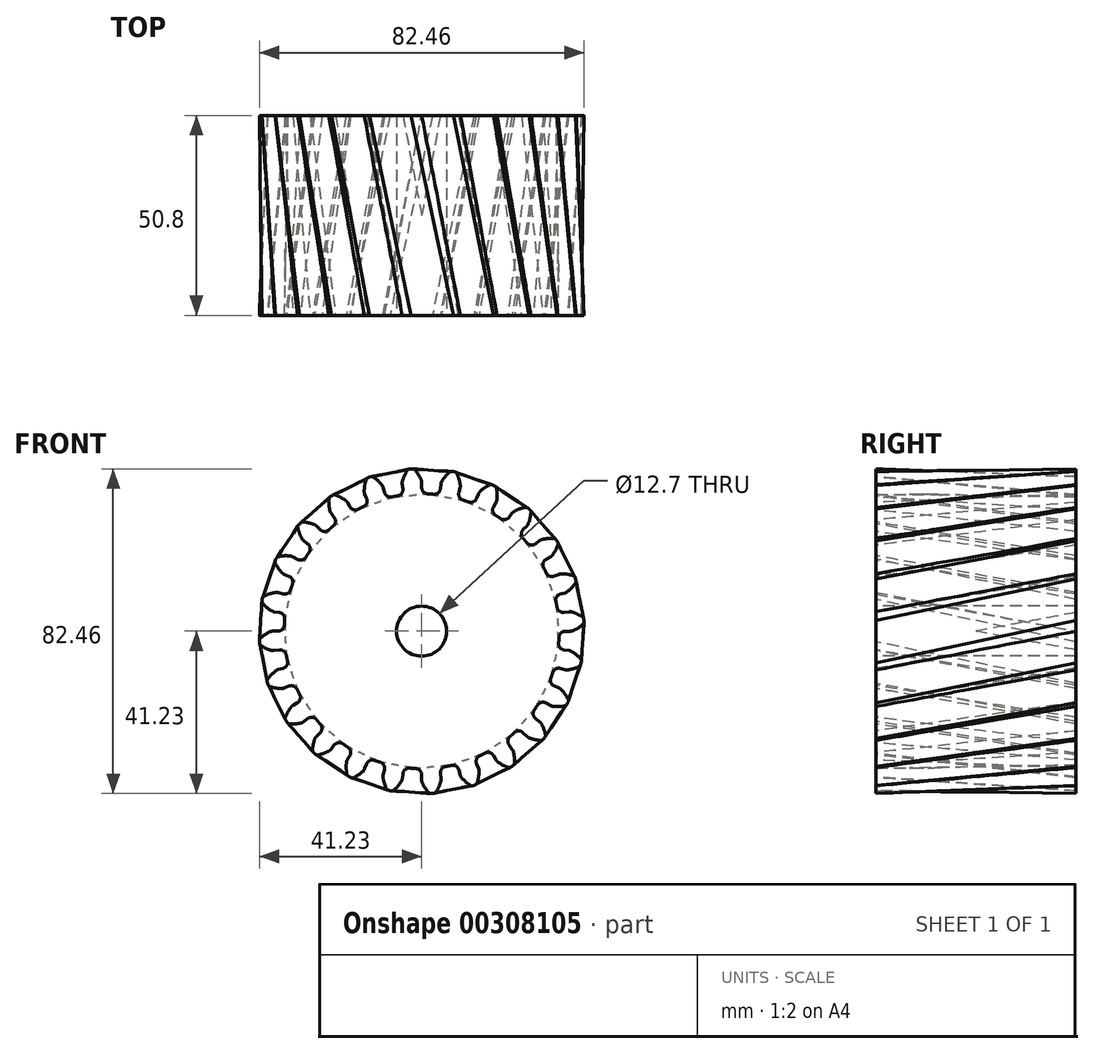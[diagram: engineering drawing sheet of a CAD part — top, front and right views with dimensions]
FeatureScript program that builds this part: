
annotation { "Feature Type Name" : "Feature", "Feature Type Description" : "" }
export const myFeature = defineFeature(function(context is Context, id is Id, definition is map)
    precondition{}
    {
        {
            var Q0;
            Q0=qCreatedBy(makeId("Front.planeOp"),FACE);
            var sketch = newSketch(context, id + "F0", { "sketchPlane" : qUnion([Q0])});
            skArc(sketch, "E0", {"start": v(-6.07, 34.4) * mm, "mid": v(-6.81, 34.25) * mm, "end": v(-7.56, 34.1) * mm});
            skArc(sketch, "E1.trimOffspring", {"start": v(-0.12, 38.41) * mm, "mid": v(-0.85, 39.8) * mm, "end": v(-1.8, 41.06) * mm});
            skLineSegment(sketch, "E2", {"start": v(-2.18, 41.23) * mm, "end": v(-2.7, 41.23) * mm});
            skLineSegment(sketch, "E3", {"start": v(0, 37.8) * mm, "end": v(0, 36.48) * mm});
            skLineSegment(sketch, "E4.MirrorCS", {"start": v(-3.22, 41.16) * mm, "end": v(-2.7, 41.23) * mm});
            skArc(sketch, "E5.MirrorCS", {"start": v(-4.9, 38.1) * mm, "mid": v(-4.35, 39.58) * mm, "end": v(-3.57, 40.95) * mm});
            skLineSegment(sketch, "E6.MirrorCS", {"start": v(-4.94, 37.47) * mm, "end": v(-4.77, 36.16) * mm});
            skPoint(sketch, "E7.visualSharp", {"position": v(-3.44, 41.13) * mm});
            skArc(sketch, "E7.filletArc", {"start": v(-3.22, 41.16) * mm, "mid": v(-3.41, 41.1) * mm, "end": v(-3.57, 40.95) * mm});
            skPoint(sketch, "E8.visualSharp", {"position": v(-1.96, 41.23) * mm});
            skArc(sketch, "E8.filletArc", {"start": v(-1.8, 41.06) * mm, "mid": v(-1.98, 41.18) * mm, "end": v(-2.18, 41.23) * mm});
            skPoint(sketch, "E9.visualSharp", {"position": v(-4.98, 37.77) * mm});
            skArc(sketch, "E9.filletArc", {"start": v(-4.9, 38.1) * mm, "mid": v(-4.95, 37.79) * mm, "end": v(-4.94, 37.47) * mm});
            skPoint(sketch, "E10.visualSharp", {"position": v(0, 38.1) * mm});
            skArc(sketch, "E10.filletArc", {"start": v(0, 37.8) * mm, "mid": v(-0.02, 38.1) * mm, "end": v(-0.12, 38.41) * mm});
            skPoint(sketch, "E11.visualSharp", {"position": v(0, 34.92) * mm});
            skArc(sketch, "E11.filletArc", {"start": v(0, 36.48) * mm, "mid": v(0.45, 35.38) * mm, "end": v(1.53, 34.9) * mm});
            skPoint(sketch, "E12.visualSharp", {"position": v(-4.57, 34.63) * mm});
            skArc(sketch, "E12.filletArc", {"start": v(-6.07, 34.4) * mm, "mid": v(-5.06, 35.02) * mm, "end": v(-4.77, 36.16) * mm});
            skLineSegment(sketch, "E13.1.0", {"start": v(-14.47, 34.91) * mm, "end": v(-13.97, 33.7) * mm});
            skArc(sketch, "E13.1.1", {"start": v(-14.76, 31.65) * mm, "mid": v(-13.95, 32.51) * mm, "end": v(-13.97, 33.7) * mm});
            skLineSegment(sketch, "E13.1.2", {"start": v(-9.77, 36.5) * mm, "end": v(-9.43, 35.24) * mm});
            skArc(sketch, "E13.1.3", {"start": v(-9.43, 35.24) * mm, "mid": v(-8.72, 34.3) * mm, "end": v(-7.56, 34.1) * mm});
            skArc(sketch, "E13.1.4", {"start": v(-14.6, 35.53) * mm, "mid": v(-14.56, 35.22) * mm, "end": v(-14.47, 34.91) * mm});
            skArc(sketch, "E13.1.5", {"start": v(-14.6, 35.53) * mm, "mid": v(-14.45, 37.1) * mm, "end": v(-14.04, 38.63) * mm});
            skArc(sketch, "E13.1.6", {"start": v(-13.76, 38.93) * mm, "mid": v(-13.93, 38.8) * mm, "end": v(-14.04, 38.63) * mm});
            skLineSegment(sketch, "E13.1.7", {"start": v(-13.76, 38.93) * mm, "end": v(-13.28, 39.12) * mm});
            skLineSegment(sketch, "E13.1.8", {"start": v(-12.78, 39.26) * mm, "end": v(-13.28, 39.12) * mm});
            skArc(sketch, "E13.1.9", {"start": v(-12.37, 39.2) * mm, "mid": v(-12.57, 39.27) * mm, "end": v(-12.78, 39.26) * mm});
            skArc(sketch, "E13.1.10", {"start": v(-10.06, 37.07) * mm, "mid": v(-11.13, 38.23) * mm, "end": v(-12.37, 39.2) * mm});
            skArc(sketch, "E13.1.11", {"start": v(-9.77, 36.5) * mm, "mid": v(-9.89, 36.8) * mm, "end": v(-10.06, 37.07) * mm});
            skLineSegment(sketch, "E13.2.0", {"start": v(-23.01, 29.98) * mm, "end": v(-22.21, 28.93) * mm});
            skArc(sketch, "E13.2.1", {"start": v(-22.45, 26.75) * mm, "mid": v(-21.9, 27.8) * mm, "end": v(-22.21, 28.93) * mm});
            skLineSegment(sketch, "E13.2.2", {"start": v(-18.89, 32.73) * mm, "end": v(-18.23, 31.6) * mm});
            skArc(sketch, "E13.2.3", {"start": v(-18.23, 31.6) * mm, "mid": v(-17.3, 30.86) * mm, "end": v(-16.12, 30.98) * mm});
            skArc(sketch, "E13.2.4", {"start": v(-23.3, 30.55) * mm, "mid": v(-23.18, 30.25) * mm, "end": v(-23.01, 29.98) * mm});
            skArc(sketch, "E13.2.5", {"start": v(-23.3, 30.55) * mm, "mid": v(-23.56, 32.1) * mm, "end": v(-23.56, 33.68) * mm});
            skArc(sketch, "E13.2.6", {"start": v(-23.36, 34.04) * mm, "mid": v(-23.5, 33.88) * mm, "end": v(-23.56, 33.68) * mm});
            skLineSegment(sketch, "E13.2.7", {"start": v(-23.36, 34.04) * mm, "end": v(-22.95, 34.35) * mm});
            skLineSegment(sketch, "E13.2.8", {"start": v(-22.5, 34.61) * mm, "end": v(-22.95, 34.35) * mm});
            skArc(sketch, "E13.2.9", {"start": v(-22.1, 34.66) * mm, "mid": v(-22.3, 34.68) * mm, "end": v(-22.5, 34.61) * mm});
            skArc(sketch, "E13.2.10", {"start": v(-19.3, 33.2) * mm, "mid": v(-20.64, 34.05) * mm, "end": v(-22.1, 34.66) * mm});
            skArc(sketch, "E13.2.11", {"start": v(-18.89, 32.73) * mm, "mid": v(-19.07, 33) * mm, "end": v(-19.3, 33.2) * mm});
            skLineSegment(sketch, "E14.2.3.0", {"start": v(-29.99, 23) * mm, "end": v(-28.94, 22.2) * mm});
            skArc(sketch, "E14.3.3.0", {"start": v(-28.61, 20.03) * mm, "mid": v(-28.34, 21.18) * mm, "end": v(-28.94, 22.2) * mm});
            skLineSegment(sketch, "E14.7.3.0", {"start": v(-26.72, 26.73) * mm, "end": v(-25.79, 25.8) * mm});
            skArc(sketch, "E14.10.3.0", {"start": v(-25.79, 25.8) * mm, "mid": v(-24.7, 25.34) * mm, "end": v(-23.6, 25.75) * mm});
            skArc(sketch, "E14.14.3.0", {"start": v(-30.4, 23.48) * mm, "mid": v(-30.22, 23.22) * mm, "end": v(-29.99, 23) * mm});
            skArc(sketch, "E14.18.3.0", {"start": v(-30.4, 23.48) * mm, "mid": v(-31.06, 24.9) * mm, "end": v(-31.48, 26.43) * mm});
            skArc(sketch, "E14.22.3.0", {"start": v(-31.38, 26.83) * mm, "mid": v(-31.47, 26.64) * mm, "end": v(-31.48, 26.43) * mm});
            skLineSegment(sketch, "E14.26.3.0", {"start": v(-31.38, 26.83) * mm, "end": v(-31.06, 27.24) * mm});
            skLineSegment(sketch, "E14.29.3.0", {"start": v(-30.7, 27.6) * mm, "end": v(-31.06, 27.24) * mm});
            skArc(sketch, "E14.32.3.0", {"start": v(-30.31, 27.76) * mm, "mid": v(-30.52, 27.72) * mm, "end": v(-30.7, 27.6) * mm});
            skArc(sketch, "E14.36.3.0", {"start": v(-27.25, 27.08) * mm, "mid": v(-28.75, 27.54) * mm, "end": v(-30.31, 27.76) * mm});
            skArc(sketch, "E14.40.3.0", {"start": v(-26.72, 26.73) * mm, "mid": v(-26.96, 26.93) * mm, "end": v(-27.25, 27.08) * mm});
            skLineSegment(sketch, "E14.2.4.0", {"start": v(-34.92, 14.45) * mm, "end": v(-33.7, 13.95) * mm});
            skArc(sketch, "E14.3.4.0", {"start": v(-32.82, 11.94) * mm, "mid": v(-32.86, 13.12) * mm, "end": v(-33.7, 13.95) * mm});
            skLineSegment(sketch, "E14.7.4.0", {"start": v(-32.72, 18.9) * mm, "end": v(-31.59, 18.25) * mm});
            skArc(sketch, "E14.10.4.0", {"start": v(-31.59, 18.25) * mm, "mid": v(-30.42, 18.08) * mm, "end": v(-29.45, 18.77) * mm});
            skArc(sketch, "E14.14.4.0", {"start": v(-35.44, 14.8) * mm, "mid": v(-35.2, 14.6) * mm, "end": v(-34.92, 14.45) * mm});
            skArc(sketch, "E14.18.4.0", {"start": v(-35.44, 14.8) * mm, "mid": v(-36.45, 16.02) * mm, "end": v(-37.24, 17.38) * mm});
            skArc(sketch, "E14.22.4.0", {"start": v(-37.25, 17.8) * mm, "mid": v(-37.3, 17.59) * mm, "end": v(-37.24, 17.38) * mm});
            skLineSegment(sketch, "E14.26.4.0", {"start": v(-37.25, 17.8) * mm, "end": v(-37.06, 18.27) * mm});
            skLineSegment(sketch, "E14.29.4.0", {"start": v(-36.8, 18.72) * mm, "end": v(-37.06, 18.27) * mm});
            skArc(sketch, "E14.32.4.0", {"start": v(-36.46, 18.96) * mm, "mid": v(-36.66, 18.88) * mm, "end": v(-36.8, 18.72) * mm});
            skArc(sketch, "E14.36.4.0", {"start": v(-33.33, 19.1) * mm, "mid": v(-34.9, 19.16) * mm, "end": v(-36.46, 18.96) * mm});
            skArc(sketch, "E14.40.4.0", {"start": v(-32.72, 18.9) * mm, "mid": v(-33.01, 19.03) * mm, "end": v(-33.33, 19.1) * mm});
            skLineSegment(sketch, "E14.2.5.0", {"start": v(-37.47, 4.92) * mm, "end": v(-36.17, 4.75) * mm});
            skArc(sketch, "E14.3.5.0", {"start": v(-34.8, 3.04) * mm, "mid": v(-35.14, 4.17) * mm, "end": v(-36.17, 4.75) * mm});
            skLineSegment(sketch, "E14.7.5.0", {"start": v(-36.5, 9.79) * mm, "end": v(-35.23, 9.45) * mm});
            skArc(sketch, "E14.10.5.0", {"start": v(-35.23, 9.45) * mm, "mid": v(-34.06, 9.6) * mm, "end": v(-33.3, 10.5) * mm});
            skArc(sketch, "E14.14.5.0", {"start": v(-38.07, 5.13) * mm, "mid": v(-37.78, 5) * mm, "end": v(-37.47, 4.92) * mm});
            skArc(sketch, "E14.18.5.0", {"start": v(-38.07, 5.13) * mm, "mid": v(-39.36, 6.04) * mm, "end": v(-40.47, 7.15) * mm});
            skArc(sketch, "E14.22.5.0", {"start": v(-40.6, 7.55) * mm, "mid": v(-40.57, 7.34) * mm, "end": v(-40.47, 7.15) * mm});
            skLineSegment(sketch, "E14.26.5.0", {"start": v(-40.6, 7.55) * mm, "end": v(-40.52, 8.06) * mm});
            skLineSegment(sketch, "E14.29.5.0", {"start": v(-40.39, 8.56) * mm, "end": v(-40.52, 8.06) * mm});
            skArc(sketch, "E14.32.5.0", {"start": v(-40.13, 8.88) * mm, "mid": v(-40.3, 8.75) * mm, "end": v(-40.39, 8.56) * mm});
            skArc(sketch, "E14.36.5.0", {"start": v(-37.13, 9.83) * mm, "mid": v(-38.67, 9.48) * mm, "end": v(-40.13, 8.88) * mm});
            skArc(sketch, "E14.40.5.0", {"start": v(-36.5, 9.79) * mm, "mid": v(-36.82, 9.84) * mm, "end": v(-37.13, 9.83) * mm});
            skLineSegment(sketch, "E14.2.6.0", {"start": v(-37.47, -4.94) * mm, "end": v(-36.16, -4.77) * mm});
            skArc(sketch, "E14.3.6.0", {"start": v(-34.4, -6.07) * mm, "mid": v(-35.02, -5.06) * mm, "end": v(-36.16, -4.77) * mm});
            skLineSegment(sketch, "E14.7.6.0", {"start": v(-37.8, 0) * mm, "end": v(-36.48, 0) * mm});
            skArc(sketch, "E14.10.6.0", {"start": v(-36.48, 0) * mm, "mid": v(-35.38, 0.45) * mm, "end": v(-34.9, 1.53) * mm});
            skArc(sketch, "E14.14.6.0", {"start": v(-38.1, -4.9) * mm, "mid": v(-37.79, -4.95) * mm, "end": v(-37.47, -4.94) * mm});
            skArc(sketch, "E14.18.6.0", {"start": v(-38.1, -4.9) * mm, "mid": v(-39.58, -4.35) * mm, "end": v(-40.95, -3.57) * mm});
            skArc(sketch, "E14.22.6.0", {"start": v(-41.16, -3.22) * mm, "mid": v(-41.1, -3.41) * mm, "end": v(-40.95, -3.57) * mm});
            skLineSegment(sketch, "E14.26.6.0", {"start": v(-41.16, -3.22) * mm, "end": v(-41.23, -2.7) * mm});
            skLineSegment(sketch, "E14.29.6.0", {"start": v(-41.23, -2.18) * mm, "end": v(-41.23, -2.7) * mm});
            skArc(sketch, "E14.32.6.0", {"start": v(-41.06, -1.8) * mm, "mid": v(-41.18, -1.98) * mm, "end": v(-41.23, -2.18) * mm});
            skArc(sketch, "E14.36.6.0", {"start": v(-38.41, -0.12) * mm, "mid": v(-39.8, -0.85) * mm, "end": v(-41.06, -1.8) * mm});
            skArc(sketch, "E14.40.6.0", {"start": v(-37.8, 0) * mm, "mid": v(-38.1, -0.02) * mm, "end": v(-38.41, -0.12) * mm});
            skLineSegment(sketch, "E14.2.7.0", {"start": v(-34.91, -14.47) * mm, "end": v(-33.7, -13.97) * mm});
            skArc(sketch, "E14.3.7.0", {"start": v(-31.65, -14.76) * mm, "mid": v(-32.51, -13.95) * mm, "end": v(-33.7, -13.97) * mm});
            skLineSegment(sketch, "E14.7.7.0", {"start": v(-36.5, -9.77) * mm, "end": v(-35.24, -9.43) * mm});
            skArc(sketch, "E14.10.7.0", {"start": v(-35.24, -9.43) * mm, "mid": v(-34.3, -8.72) * mm, "end": v(-34.1, -7.56) * mm});
            skArc(sketch, "E14.14.7.0", {"start": v(-35.53, -14.6) * mm, "mid": v(-35.22, -14.56) * mm, "end": v(-34.91, -14.47) * mm});
            skArc(sketch, "E14.18.7.0", {"start": v(-35.53, -14.6) * mm, "mid": v(-37.1, -14.45) * mm, "end": v(-38.63, -14.04) * mm});
            skArc(sketch, "E14.22.7.0", {"start": v(-38.93, -13.76) * mm, "mid": v(-38.8, -13.93) * mm, "end": v(-38.63, -14.04) * mm});
            skLineSegment(sketch, "E14.26.7.0", {"start": v(-38.93, -13.76) * mm, "end": v(-39.12, -13.28) * mm});
            skLineSegment(sketch, "E14.29.7.0", {"start": v(-39.26, -12.78) * mm, "end": v(-39.12, -13.28) * mm});
            skArc(sketch, "E14.32.7.0", {"start": v(-39.2, -12.37) * mm, "mid": v(-39.27, -12.57) * mm, "end": v(-39.26, -12.78) * mm});
            skArc(sketch, "E14.36.7.0", {"start": v(-37.07, -10.06) * mm, "mid": v(-38.23, -11.13) * mm, "end": v(-39.2, -12.37) * mm});
            skArc(sketch, "E14.40.7.0", {"start": v(-36.5, -9.77) * mm, "mid": v(-36.8, -9.89) * mm, "end": v(-37.07, -10.06) * mm});
            skLineSegment(sketch, "E14.2.8.0", {"start": v(-29.98, -23.01) * mm, "end": v(-28.93, -22.21) * mm});
            skArc(sketch, "E14.3.8.0", {"start": v(-26.75, -22.45) * mm, "mid": v(-27.8, -21.9) * mm, "end": v(-28.93, -22.21) * mm});
            skLineSegment(sketch, "E14.7.8.0", {"start": v(-32.73, -18.89) * mm, "end": v(-31.6, -18.23) * mm});
            skArc(sketch, "E14.10.8.0", {"start": v(-31.6, -18.23) * mm, "mid": v(-30.86, -17.3) * mm, "end": v(-30.98, -16.12) * mm});
            skArc(sketch, "E14.14.8.0", {"start": v(-30.55, -23.3) * mm, "mid": v(-30.25, -23.18) * mm, "end": v(-29.98, -23.01) * mm});
            skArc(sketch, "E14.18.8.0", {"start": v(-30.55, -23.3) * mm, "mid": v(-32.1, -23.56) * mm, "end": v(-33.68, -23.56) * mm});
            skArc(sketch, "E14.22.8.0", {"start": v(-34.04, -23.36) * mm, "mid": v(-33.88, -23.5) * mm, "end": v(-33.68, -23.56) * mm});
            skLineSegment(sketch, "E14.26.8.0", {"start": v(-34.04, -23.36) * mm, "end": v(-34.35, -22.95) * mm});
            skLineSegment(sketch, "E14.29.8.0", {"start": v(-34.61, -22.5) * mm, "end": v(-34.35, -22.95) * mm});
            skArc(sketch, "E14.32.8.0", {"start": v(-34.66, -22.1) * mm, "mid": v(-34.68, -22.3) * mm, "end": v(-34.61, -22.5) * mm});
            skArc(sketch, "E14.36.8.0", {"start": v(-33.2, -19.3) * mm, "mid": v(-34.05, -20.64) * mm, "end": v(-34.66, -22.1) * mm});
            skArc(sketch, "E14.40.8.0", {"start": v(-32.73, -18.89) * mm, "mid": v(-33, -19.07) * mm, "end": v(-33.2, -19.3) * mm});
            skLineSegment(sketch, "E14.2.9.0", {"start": v(-23, -29.99) * mm, "end": v(-22.2, -28.94) * mm});
            skArc(sketch, "E14.3.9.0", {"start": v(-20.03, -28.61) * mm, "mid": v(-21.18, -28.34) * mm, "end": v(-22.2, -28.94) * mm});
            skLineSegment(sketch, "E14.7.9.0", {"start": v(-26.73, -26.72) * mm, "end": v(-25.8, -25.79) * mm});
            skArc(sketch, "E14.10.9.0", {"start": v(-25.8, -25.79) * mm, "mid": v(-25.34, -24.7) * mm, "end": v(-25.75, -23.6) * mm});
            skArc(sketch, "E14.14.9.0", {"start": v(-23.48, -30.4) * mm, "mid": v(-23.22, -30.22) * mm, "end": v(-23, -29.99) * mm});
            skArc(sketch, "E14.18.9.0", {"start": v(-23.48, -30.4) * mm, "mid": v(-24.9, -31.06) * mm, "end": v(-26.43, -31.48) * mm});
            skArc(sketch, "E14.22.9.0", {"start": v(-26.83, -31.38) * mm, "mid": v(-26.64, -31.47) * mm, "end": v(-26.43, -31.48) * mm});
            skLineSegment(sketch, "E14.26.9.0", {"start": v(-26.83, -31.38) * mm, "end": v(-27.24, -31.06) * mm});
            skLineSegment(sketch, "E14.29.9.0", {"start": v(-27.6, -30.7) * mm, "end": v(-27.24, -31.06) * mm});
            skArc(sketch, "E14.32.9.0", {"start": v(-27.76, -30.31) * mm, "mid": v(-27.72, -30.52) * mm, "end": v(-27.6, -30.7) * mm});
            skArc(sketch, "E14.36.9.0", {"start": v(-27.08, -27.25) * mm, "mid": v(-27.54, -28.75) * mm, "end": v(-27.76, -30.31) * mm});
            skArc(sketch, "E14.40.9.0", {"start": v(-26.73, -26.72) * mm, "mid": v(-26.93, -26.96) * mm, "end": v(-27.08, -27.25) * mm});
            skLineSegment(sketch, "E14.2.10.0", {"start": v(-14.45, -34.92) * mm, "end": v(-13.95, -33.7) * mm});
            skArc(sketch, "E14.3.10.0", {"start": v(-11.94, -32.82) * mm, "mid": v(-13.12, -32.86) * mm, "end": v(-13.95, -33.7) * mm});
            skLineSegment(sketch, "E14.7.10.0", {"start": v(-18.9, -32.72) * mm, "end": v(-18.25, -31.59) * mm});
            skArc(sketch, "E14.10.10.0", {"start": v(-18.25, -31.59) * mm, "mid": v(-18.08, -30.42) * mm, "end": v(-18.77, -29.45) * mm});
            skArc(sketch, "E14.14.10.0", {"start": v(-14.8, -35.44) * mm, "mid": v(-14.6, -35.2) * mm, "end": v(-14.45, -34.92) * mm});
            skArc(sketch, "E14.18.10.0", {"start": v(-14.8, -35.44) * mm, "mid": v(-16.02, -36.45) * mm, "end": v(-17.38, -37.24) * mm});
            skArc(sketch, "E14.22.10.0", {"start": v(-17.8, -37.25) * mm, "mid": v(-17.59, -37.3) * mm, "end": v(-17.38, -37.24) * mm});
            skLineSegment(sketch, "E14.26.10.0", {"start": v(-17.8, -37.25) * mm, "end": v(-18.27, -37.06) * mm});
            skLineSegment(sketch, "E14.29.10.0", {"start": v(-18.72, -36.8) * mm, "end": v(-18.27, -37.06) * mm});
            skArc(sketch, "E14.32.10.0", {"start": v(-18.96, -36.46) * mm, "mid": v(-18.88, -36.66) * mm, "end": v(-18.72, -36.8) * mm});
            skArc(sketch, "E14.36.10.0", {"start": v(-19.1, -33.33) * mm, "mid": v(-19.16, -34.9) * mm, "end": v(-18.96, -36.46) * mm});
            skArc(sketch, "E14.40.10.0", {"start": v(-18.9, -32.72) * mm, "mid": v(-19.03, -33.01) * mm, "end": v(-19.1, -33.33) * mm});
            skLineSegment(sketch, "E14.2.11.0", {"start": v(-4.92, -37.47) * mm, "end": v(-4.75, -36.17) * mm});
            skArc(sketch, "E14.3.11.0", {"start": v(-3.04, -34.8) * mm, "mid": v(-4.17, -35.14) * mm, "end": v(-4.75, -36.17) * mm});
            skLineSegment(sketch, "E14.7.11.0", {"start": v(-9.79, -36.5) * mm, "end": v(-9.45, -35.23) * mm});
            skArc(sketch, "E14.10.11.0", {"start": v(-9.45, -35.23) * mm, "mid": v(-9.6, -34.06) * mm, "end": v(-10.5, -33.3) * mm});
            skArc(sketch, "E14.14.11.0", {"start": v(-5.13, -38.07) * mm, "mid": v(-5, -37.78) * mm, "end": v(-4.92, -37.47) * mm});
            skArc(sketch, "E14.18.11.0", {"start": v(-5.13, -38.07) * mm, "mid": v(-6.04, -39.36) * mm, "end": v(-7.15, -40.47) * mm});
            skArc(sketch, "E14.22.11.0", {"start": v(-7.55, -40.6) * mm, "mid": v(-7.34, -40.57) * mm, "end": v(-7.15, -40.47) * mm});
            skLineSegment(sketch, "E14.26.11.0", {"start": v(-7.55, -40.6) * mm, "end": v(-8.06, -40.52) * mm});
            skLineSegment(sketch, "E14.29.11.0", {"start": v(-8.56, -40.39) * mm, "end": v(-8.06, -40.52) * mm});
            skArc(sketch, "E14.32.11.0", {"start": v(-8.88, -40.13) * mm, "mid": v(-8.75, -40.3) * mm, "end": v(-8.56, -40.39) * mm});
            skArc(sketch, "E14.36.11.0", {"start": v(-9.83, -37.13) * mm, "mid": v(-9.48, -38.67) * mm, "end": v(-8.88, -40.13) * mm});
            skArc(sketch, "E14.40.11.0", {"start": v(-9.79, -36.5) * mm, "mid": v(-9.84, -36.82) * mm, "end": v(-9.83, -37.13) * mm});
            skLineSegment(sketch, "E14.2.12.0", {"start": v(4.94, -37.47) * mm, "end": v(4.77, -36.16) * mm});
            skArc(sketch, "E14.3.12.0", {"start": v(6.07, -34.4) * mm, "mid": v(5.06, -35.02) * mm, "end": v(4.77, -36.16) * mm});
            skLineSegment(sketch, "E14.7.12.0", {"start": v(0, -37.8) * mm, "end": v(0, -36.48) * mm});
            skArc(sketch, "E14.10.12.0", {"start": v(0, -36.48) * mm, "mid": v(-0.45, -35.38) * mm, "end": v(-1.53, -34.9) * mm});
            skArc(sketch, "E14.14.12.0", {"start": v(4.9, -38.1) * mm, "mid": v(4.95, -37.79) * mm, "end": v(4.94, -37.47) * mm});
            skArc(sketch, "E14.18.12.0", {"start": v(4.9, -38.1) * mm, "mid": v(4.35, -39.58) * mm, "end": v(3.57, -40.95) * mm});
            skArc(sketch, "E14.22.12.0", {"start": v(3.22, -41.16) * mm, "mid": v(3.41, -41.1) * mm, "end": v(3.57, -40.95) * mm});
            skLineSegment(sketch, "E14.26.12.0", {"start": v(3.22, -41.16) * mm, "end": v(2.7, -41.23) * mm});
            skLineSegment(sketch, "E14.29.12.0", {"start": v(2.18, -41.23) * mm, "end": v(2.7, -41.23) * mm});
            skArc(sketch, "E14.32.12.0", {"start": v(1.8, -41.06) * mm, "mid": v(1.98, -41.18) * mm, "end": v(2.18, -41.23) * mm});
            skArc(sketch, "E14.36.12.0", {"start": v(0.12, -38.41) * mm, "mid": v(0.85, -39.8) * mm, "end": v(1.8, -41.06) * mm});
            skArc(sketch, "E14.40.12.0", {"start": v(0, -37.8) * mm, "mid": v(0.02, -38.1) * mm, "end": v(0.12, -38.41) * mm});
            skLineSegment(sketch, "E14.2.13.0", {"start": v(14.47, -34.91) * mm, "end": v(13.97, -33.7) * mm});
            skArc(sketch, "E14.3.13.0", {"start": v(14.76, -31.65) * mm, "mid": v(13.95, -32.51) * mm, "end": v(13.97, -33.7) * mm});
            skLineSegment(sketch, "E14.7.13.0", {"start": v(9.77, -36.5) * mm, "end": v(9.43, -35.24) * mm});
            skArc(sketch, "E14.10.13.0", {"start": v(9.43, -35.24) * mm, "mid": v(8.72, -34.3) * mm, "end": v(7.56, -34.1) * mm});
            skArc(sketch, "E14.14.13.0", {"start": v(14.6, -35.53) * mm, "mid": v(14.56, -35.22) * mm, "end": v(14.47, -34.91) * mm});
            skArc(sketch, "E14.18.13.0", {"start": v(14.6, -35.53) * mm, "mid": v(14.45, -37.1) * mm, "end": v(14.04, -38.63) * mm});
            skArc(sketch, "E14.22.13.0", {"start": v(13.76, -38.93) * mm, "mid": v(13.93, -38.8) * mm, "end": v(14.04, -38.63) * mm});
            skLineSegment(sketch, "E14.26.13.0", {"start": v(13.76, -38.93) * mm, "end": v(13.28, -39.12) * mm});
            skLineSegment(sketch, "E14.29.13.0", {"start": v(12.78, -39.26) * mm, "end": v(13.28, -39.12) * mm});
            skArc(sketch, "E14.32.13.0", {"start": v(12.37, -39.2) * mm, "mid": v(12.57, -39.27) * mm, "end": v(12.78, -39.26) * mm});
            skArc(sketch, "E14.36.13.0", {"start": v(10.06, -37.07) * mm, "mid": v(11.13, -38.23) * mm, "end": v(12.37, -39.2) * mm});
            skArc(sketch, "E14.40.13.0", {"start": v(9.77, -36.5) * mm, "mid": v(9.89, -36.8) * mm, "end": v(10.06, -37.07) * mm});
            skLineSegment(sketch, "E14.2.14.0", {"start": v(23.01, -29.98) * mm, "end": v(22.21, -28.93) * mm});
            skArc(sketch, "E14.3.14.0", {"start": v(22.45, -26.75) * mm, "mid": v(21.9, -27.8) * mm, "end": v(22.21, -28.93) * mm});
            skLineSegment(sketch, "E14.7.14.0", {"start": v(18.89, -32.73) * mm, "end": v(18.23, -31.6) * mm});
            skArc(sketch, "E14.10.14.0", {"start": v(18.23, -31.6) * mm, "mid": v(17.3, -30.86) * mm, "end": v(16.12, -30.98) * mm});
            skArc(sketch, "E14.14.14.0", {"start": v(23.3, -30.55) * mm, "mid": v(23.18, -30.25) * mm, "end": v(23.01, -29.98) * mm});
            skArc(sketch, "E14.18.14.0", {"start": v(23.3, -30.55) * mm, "mid": v(23.56, -32.1) * mm, "end": v(23.56, -33.68) * mm});
            skArc(sketch, "E14.22.14.0", {"start": v(23.36, -34.04) * mm, "mid": v(23.5, -33.88) * mm, "end": v(23.56, -33.68) * mm});
            skLineSegment(sketch, "E14.26.14.0", {"start": v(23.36, -34.04) * mm, "end": v(22.95, -34.35) * mm});
            skLineSegment(sketch, "E14.29.14.0", {"start": v(22.5, -34.61) * mm, "end": v(22.95, -34.35) * mm});
            skArc(sketch, "E14.32.14.0", {"start": v(22.1, -34.66) * mm, "mid": v(22.3, -34.68) * mm, "end": v(22.5, -34.61) * mm});
            skArc(sketch, "E14.36.14.0", {"start": v(19.3, -33.2) * mm, "mid": v(20.64, -34.05) * mm, "end": v(22.1, -34.66) * mm});
            skArc(sketch, "E14.40.14.0", {"start": v(18.89, -32.73) * mm, "mid": v(19.07, -33) * mm, "end": v(19.3, -33.2) * mm});
            skLineSegment(sketch, "E14.2.15.0", {"start": v(29.99, -23) * mm, "end": v(28.94, -22.2) * mm});
            skArc(sketch, "E14.3.15.0", {"start": v(28.61, -20.03) * mm, "mid": v(28.34, -21.18) * mm, "end": v(28.94, -22.2) * mm});
            skLineSegment(sketch, "E14.7.15.0", {"start": v(26.72, -26.73) * mm, "end": v(25.79, -25.8) * mm});
            skArc(sketch, "E14.10.15.0", {"start": v(25.79, -25.8) * mm, "mid": v(24.7, -25.34) * mm, "end": v(23.6, -25.75) * mm});
            skArc(sketch, "E14.14.15.0", {"start": v(30.4, -23.48) * mm, "mid": v(30.22, -23.22) * mm, "end": v(29.99, -23) * mm});
            skArc(sketch, "E14.18.15.0", {"start": v(30.4, -23.48) * mm, "mid": v(31.06, -24.9) * mm, "end": v(31.48, -26.43) * mm});
            skArc(sketch, "E14.22.15.0", {"start": v(31.38, -26.83) * mm, "mid": v(31.47, -26.64) * mm, "end": v(31.48, -26.43) * mm});
            skLineSegment(sketch, "E14.26.15.0", {"start": v(31.38, -26.83) * mm, "end": v(31.06, -27.24) * mm});
            skLineSegment(sketch, "E14.29.15.0", {"start": v(30.7, -27.6) * mm, "end": v(31.06, -27.24) * mm});
            skArc(sketch, "E14.32.15.0", {"start": v(30.31, -27.76) * mm, "mid": v(30.52, -27.72) * mm, "end": v(30.7, -27.6) * mm});
            skArc(sketch, "E14.36.15.0", {"start": v(27.25, -27.08) * mm, "mid": v(28.75, -27.54) * mm, "end": v(30.31, -27.76) * mm});
            skArc(sketch, "E14.40.15.0", {"start": v(26.72, -26.73) * mm, "mid": v(26.96, -26.93) * mm, "end": v(27.25, -27.08) * mm});
            skLineSegment(sketch, "E14.2.16.0", {"start": v(34.92, -14.45) * mm, "end": v(33.7, -13.95) * mm});
            skArc(sketch, "E14.3.16.0", {"start": v(32.82, -11.94) * mm, "mid": v(32.86, -13.12) * mm, "end": v(33.7, -13.95) * mm});
            skLineSegment(sketch, "E14.7.16.0", {"start": v(32.72, -18.9) * mm, "end": v(31.59, -18.25) * mm});
            skArc(sketch, "E14.10.16.0", {"start": v(31.59, -18.25) * mm, "mid": v(30.42, -18.08) * mm, "end": v(29.45, -18.77) * mm});
            skArc(sketch, "E14.14.16.0", {"start": v(35.44, -14.8) * mm, "mid": v(35.2, -14.6) * mm, "end": v(34.92, -14.45) * mm});
            skArc(sketch, "E14.18.16.0", {"start": v(35.44, -14.8) * mm, "mid": v(36.45, -16.02) * mm, "end": v(37.24, -17.38) * mm});
            skArc(sketch, "E14.22.16.0", {"start": v(37.25, -17.8) * mm, "mid": v(37.3, -17.59) * mm, "end": v(37.24, -17.38) * mm});
            skLineSegment(sketch, "E14.26.16.0", {"start": v(37.25, -17.8) * mm, "end": v(37.06, -18.27) * mm});
            skLineSegment(sketch, "E14.29.16.0", {"start": v(36.8, -18.72) * mm, "end": v(37.06, -18.27) * mm});
            skArc(sketch, "E14.32.16.0", {"start": v(36.46, -18.96) * mm, "mid": v(36.66, -18.88) * mm, "end": v(36.8, -18.72) * mm});
            skArc(sketch, "E14.36.16.0", {"start": v(33.33, -19.1) * mm, "mid": v(34.9, -19.16) * mm, "end": v(36.46, -18.96) * mm});
            skArc(sketch, "E14.40.16.0", {"start": v(32.72, -18.9) * mm, "mid": v(33.01, -19.03) * mm, "end": v(33.33, -19.1) * mm});
            skLineSegment(sketch, "E14.2.17.0", {"start": v(37.47, -4.92) * mm, "end": v(36.17, -4.75) * mm});
            skArc(sketch, "E14.3.17.0", {"start": v(34.8, -3.04) * mm, "mid": v(35.14, -4.17) * mm, "end": v(36.17, -4.75) * mm});
            skLineSegment(sketch, "E14.7.17.0", {"start": v(36.5, -9.79) * mm, "end": v(35.23, -9.45) * mm});
            skArc(sketch, "E14.10.17.0", {"start": v(35.23, -9.45) * mm, "mid": v(34.06, -9.6) * mm, "end": v(33.3, -10.5) * mm});
            skArc(sketch, "E14.14.17.0", {"start": v(38.07, -5.13) * mm, "mid": v(37.78, -5) * mm, "end": v(37.47, -4.92) * mm});
            skArc(sketch, "E14.18.17.0", {"start": v(38.07, -5.13) * mm, "mid": v(39.36, -6.04) * mm, "end": v(40.47, -7.15) * mm});
            skArc(sketch, "E14.22.17.0", {"start": v(40.6, -7.55) * mm, "mid": v(40.57, -7.34) * mm, "end": v(40.47, -7.15) * mm});
            skLineSegment(sketch, "E14.26.17.0", {"start": v(40.6, -7.55) * mm, "end": v(40.52, -8.06) * mm});
            skLineSegment(sketch, "E14.29.17.0", {"start": v(40.39, -8.56) * mm, "end": v(40.52, -8.06) * mm});
            skArc(sketch, "E14.32.17.0", {"start": v(40.13, -8.88) * mm, "mid": v(40.3, -8.75) * mm, "end": v(40.39, -8.56) * mm});
            skArc(sketch, "E14.36.17.0", {"start": v(37.13, -9.83) * mm, "mid": v(38.67, -9.48) * mm, "end": v(40.13, -8.88) * mm});
            skArc(sketch, "E14.40.17.0", {"start": v(36.5, -9.79) * mm, "mid": v(36.82, -9.84) * mm, "end": v(37.13, -9.83) * mm});
            skLineSegment(sketch, "E14.2.18.0", {"start": v(37.47, 4.94) * mm, "end": v(36.16, 4.77) * mm});
            skArc(sketch, "E14.3.18.0", {"start": v(34.4, 6.07) * mm, "mid": v(35.02, 5.06) * mm, "end": v(36.16, 4.77) * mm});
            skLineSegment(sketch, "E14.7.18.0", {"start": v(37.8, 0) * mm, "end": v(36.48, 0) * mm});
            skArc(sketch, "E14.10.18.0", {"start": v(36.48, 0) * mm, "mid": v(35.38, -0.45) * mm, "end": v(34.9, -1.53) * mm});
            skArc(sketch, "E14.14.18.0", {"start": v(38.1, 4.9) * mm, "mid": v(37.79, 4.95) * mm, "end": v(37.47, 4.94) * mm});
            skArc(sketch, "E14.18.18.0", {"start": v(38.1, 4.9) * mm, "mid": v(39.58, 4.35) * mm, "end": v(40.95, 3.57) * mm});
            skArc(sketch, "E14.22.18.0", {"start": v(41.16, 3.22) * mm, "mid": v(41.1, 3.41) * mm, "end": v(40.95, 3.57) * mm});
            skLineSegment(sketch, "E14.26.18.0", {"start": v(41.16, 3.22) * mm, "end": v(41.23, 2.7) * mm});
            skLineSegment(sketch, "E14.29.18.0", {"start": v(41.23, 2.18) * mm, "end": v(41.23, 2.7) * mm});
            skArc(sketch, "E14.32.18.0", {"start": v(41.06, 1.8) * mm, "mid": v(41.18, 1.98) * mm, "end": v(41.23, 2.18) * mm});
            skArc(sketch, "E14.36.18.0", {"start": v(38.41, 0.12) * mm, "mid": v(39.8, 0.85) * mm, "end": v(41.06, 1.8) * mm});
            skArc(sketch, "E14.40.18.0", {"start": v(37.8, 0) * mm, "mid": v(38.1, 0.02) * mm, "end": v(38.41, 0.12) * mm});
            skLineSegment(sketch, "E14.2.19.0", {"start": v(34.91, 14.47) * mm, "end": v(33.7, 13.97) * mm});
            skArc(sketch, "E14.3.19.0", {"start": v(31.65, 14.76) * mm, "mid": v(32.51, 13.95) * mm, "end": v(33.7, 13.97) * mm});
            skLineSegment(sketch, "E14.7.19.0", {"start": v(36.5, 9.77) * mm, "end": v(35.24, 9.43) * mm});
            skArc(sketch, "E14.10.19.0", {"start": v(35.24, 9.43) * mm, "mid": v(34.3, 8.72) * mm, "end": v(34.1, 7.56) * mm});
            skArc(sketch, "E14.14.19.0", {"start": v(35.53, 14.6) * mm, "mid": v(35.22, 14.56) * mm, "end": v(34.91, 14.47) * mm});
            skArc(sketch, "E14.18.19.0", {"start": v(35.53, 14.6) * mm, "mid": v(37.1, 14.45) * mm, "end": v(38.63, 14.04) * mm});
            skArc(sketch, "E14.22.19.0", {"start": v(38.93, 13.76) * mm, "mid": v(38.8, 13.93) * mm, "end": v(38.63, 14.04) * mm});
            skLineSegment(sketch, "E14.26.19.0", {"start": v(38.93, 13.76) * mm, "end": v(39.12, 13.28) * mm});
            skLineSegment(sketch, "E14.29.19.0", {"start": v(39.26, 12.78) * mm, "end": v(39.12, 13.28) * mm});
            skArc(sketch, "E14.32.19.0", {"start": v(39.2, 12.37) * mm, "mid": v(39.27, 12.57) * mm, "end": v(39.26, 12.78) * mm});
            skArc(sketch, "E14.36.19.0", {"start": v(37.07, 10.06) * mm, "mid": v(38.23, 11.13) * mm, "end": v(39.2, 12.37) * mm});
            skArc(sketch, "E14.40.19.0", {"start": v(36.5, 9.77) * mm, "mid": v(36.8, 9.89) * mm, "end": v(37.07, 10.06) * mm});
            skLineSegment(sketch, "E14.2.20.0", {"start": v(29.98, 23.01) * mm, "end": v(28.93, 22.21) * mm});
            skArc(sketch, "E14.3.20.0", {"start": v(26.75, 22.45) * mm, "mid": v(27.8, 21.9) * mm, "end": v(28.93, 22.21) * mm});
            skLineSegment(sketch, "E14.7.20.0", {"start": v(32.73, 18.89) * mm, "end": v(31.6, 18.23) * mm});
            skArc(sketch, "E14.10.20.0", {"start": v(31.6, 18.23) * mm, "mid": v(30.86, 17.3) * mm, "end": v(30.98, 16.12) * mm});
            skArc(sketch, "E14.14.20.0", {"start": v(30.55, 23.3) * mm, "mid": v(30.25, 23.18) * mm, "end": v(29.98, 23.01) * mm});
            skArc(sketch, "E14.18.20.0", {"start": v(30.55, 23.3) * mm, "mid": v(32.1, 23.56) * mm, "end": v(33.68, 23.56) * mm});
            skArc(sketch, "E14.22.20.0", {"start": v(34.04, 23.36) * mm, "mid": v(33.88, 23.5) * mm, "end": v(33.68, 23.56) * mm});
            skLineSegment(sketch, "E14.26.20.0", {"start": v(34.04, 23.36) * mm, "end": v(34.35, 22.95) * mm});
            skLineSegment(sketch, "E14.29.20.0", {"start": v(34.61, 22.5) * mm, "end": v(34.35, 22.95) * mm});
            skArc(sketch, "E14.32.20.0", {"start": v(34.66, 22.1) * mm, "mid": v(34.68, 22.3) * mm, "end": v(34.61, 22.5) * mm});
            skArc(sketch, "E14.36.20.0", {"start": v(33.2, 19.3) * mm, "mid": v(34.05, 20.64) * mm, "end": v(34.66, 22.1) * mm});
            skArc(sketch, "E14.40.20.0", {"start": v(32.73, 18.89) * mm, "mid": v(33, 19.07) * mm, "end": v(33.2, 19.3) * mm});
            skLineSegment(sketch, "E14.2.21.0", {"start": v(23, 29.99) * mm, "end": v(22.2, 28.94) * mm});
            skArc(sketch, "E14.3.21.0", {"start": v(20.03, 28.61) * mm, "mid": v(21.18, 28.34) * mm, "end": v(22.2, 28.94) * mm});
            skLineSegment(sketch, "E14.7.21.0", {"start": v(26.73, 26.72) * mm, "end": v(25.8, 25.79) * mm});
            skArc(sketch, "E14.10.21.0", {"start": v(25.8, 25.79) * mm, "mid": v(25.34, 24.7) * mm, "end": v(25.75, 23.6) * mm});
            skArc(sketch, "E14.14.21.0", {"start": v(23.48, 30.4) * mm, "mid": v(23.22, 30.22) * mm, "end": v(23, 29.99) * mm});
            skArc(sketch, "E14.18.21.0", {"start": v(23.48, 30.4) * mm, "mid": v(24.9, 31.06) * mm, "end": v(26.43, 31.48) * mm});
            skArc(sketch, "E14.22.21.0", {"start": v(26.83, 31.38) * mm, "mid": v(26.64, 31.47) * mm, "end": v(26.43, 31.48) * mm});
            skLineSegment(sketch, "E14.26.21.0", {"start": v(26.83, 31.38) * mm, "end": v(27.24, 31.06) * mm});
            skLineSegment(sketch, "E14.29.21.0", {"start": v(27.6, 30.7) * mm, "end": v(27.24, 31.06) * mm});
            skArc(sketch, "E14.32.21.0", {"start": v(27.76, 30.31) * mm, "mid": v(27.72, 30.52) * mm, "end": v(27.6, 30.7) * mm});
            skArc(sketch, "E14.36.21.0", {"start": v(27.08, 27.25) * mm, "mid": v(27.54, 28.75) * mm, "end": v(27.76, 30.31) * mm});
            skArc(sketch, "E14.40.21.0", {"start": v(26.73, 26.72) * mm, "mid": v(26.93, 26.96) * mm, "end": v(27.08, 27.25) * mm});
            skLineSegment(sketch, "E14.2.22.0", {"start": v(14.45, 34.92) * mm, "end": v(13.95, 33.7) * mm});
            skArc(sketch, "E14.3.22.0", {"start": v(11.94, 32.82) * mm, "mid": v(13.12, 32.86) * mm, "end": v(13.95, 33.7) * mm});
            skLineSegment(sketch, "E14.7.22.0", {"start": v(18.9, 32.72) * mm, "end": v(18.25, 31.59) * mm});
            skArc(sketch, "E14.10.22.0", {"start": v(18.25, 31.59) * mm, "mid": v(18.08, 30.42) * mm, "end": v(18.77, 29.45) * mm});
            skArc(sketch, "E14.14.22.0", {"start": v(14.8, 35.44) * mm, "mid": v(14.6, 35.2) * mm, "end": v(14.45, 34.92) * mm});
            skArc(sketch, "E14.18.22.0", {"start": v(14.8, 35.44) * mm, "mid": v(16.02, 36.45) * mm, "end": v(17.38, 37.24) * mm});
            skArc(sketch, "E14.22.22.0", {"start": v(17.8, 37.25) * mm, "mid": v(17.59, 37.3) * mm, "end": v(17.38, 37.24) * mm});
            skLineSegment(sketch, "E14.26.22.0", {"start": v(17.8, 37.25) * mm, "end": v(18.27, 37.06) * mm});
            skLineSegment(sketch, "E14.29.22.0", {"start": v(18.72, 36.8) * mm, "end": v(18.27, 37.06) * mm});
            skArc(sketch, "E14.32.22.0", {"start": v(18.96, 36.46) * mm, "mid": v(18.88, 36.66) * mm, "end": v(18.72, 36.8) * mm});
            skArc(sketch, "E14.36.22.0", {"start": v(19.1, 33.33) * mm, "mid": v(19.16, 34.9) * mm, "end": v(18.96, 36.46) * mm});
            skArc(sketch, "E14.40.22.0", {"start": v(18.9, 32.72) * mm, "mid": v(19.03, 33.01) * mm, "end": v(19.1, 33.33) * mm});
            skLineSegment(sketch, "E14.2.23.0", {"start": v(4.92, 37.47) * mm, "end": v(4.75, 36.17) * mm});
            skArc(sketch, "E14.3.23.0", {"start": v(3.04, 34.8) * mm, "mid": v(4.17, 35.14) * mm, "end": v(4.75, 36.17) * mm});
            skLineSegment(sketch, "E14.7.23.0", {"start": v(9.79, 36.5) * mm, "end": v(9.45, 35.23) * mm});
            skArc(sketch, "E14.10.23.0", {"start": v(9.45, 35.23) * mm, "mid": v(9.6, 34.06) * mm, "end": v(10.5, 33.3) * mm});
            skArc(sketch, "E14.14.23.0", {"start": v(5.13, 38.07) * mm, "mid": v(5, 37.78) * mm, "end": v(4.92, 37.47) * mm});
            skArc(sketch, "E14.18.23.0", {"start": v(5.13, 38.07) * mm, "mid": v(6.04, 39.36) * mm, "end": v(7.15, 40.47) * mm});
            skArc(sketch, "E14.22.23.0", {"start": v(7.55, 40.6) * mm, "mid": v(7.34, 40.57) * mm, "end": v(7.15, 40.47) * mm});
            skLineSegment(sketch, "E14.26.23.0", {"start": v(7.55, 40.6) * mm, "end": v(8.06, 40.52) * mm});
            skLineSegment(sketch, "E14.29.23.0", {"start": v(8.56, 40.39) * mm, "end": v(8.06, 40.52) * mm});
            skArc(sketch, "E14.32.23.0", {"start": v(8.88, 40.13) * mm, "mid": v(8.75, 40.3) * mm, "end": v(8.56, 40.39) * mm});
            skArc(sketch, "E14.36.23.0", {"start": v(9.83, 37.13) * mm, "mid": v(9.48, 38.67) * mm, "end": v(8.88, 40.13) * mm});
            skArc(sketch, "E14.40.23.0", {"start": v(9.79, 36.5) * mm, "mid": v(9.84, 36.82) * mm, "end": v(9.83, 37.13) * mm});
            skArc(sketch, "E15.trimOffspring", {"start": v(-28.61, 20.03) * mm, "mid": v(-29.04, 19.4) * mm, "end": v(-29.45, 18.77) * mm});
            skArc(sketch, "E16.trimOffspring", {"start": v(-22.45, 26.75) * mm, "mid": v(-23.03, 26.26) * mm, "end": v(-23.6, 25.75) * mm});
            skArc(sketch, "E17.trimOffspring", {"start": v(-14.76, 31.65) * mm, "mid": v(-15.45, 31.32) * mm, "end": v(-16.12, 30.98) * mm});
            skArc(sketch, "E18.trimOffspring", {"start": v(3.04, 34.8) * mm, "mid": v(2.28, 34.85) * mm, "end": v(1.53, 34.9) * mm});
            skArc(sketch, "E19.trimOffspring", {"start": v(11.94, 32.82) * mm, "mid": v(11.23, 33.07) * mm, "end": v(10.5, 33.3) * mm});
            skArc(sketch, "E20.trimOffspring", {"start": v(20.03, 28.61) * mm, "mid": v(19.4, 29.04) * mm, "end": v(18.77, 29.45) * mm});
            skArc(sketch, "E21.trimOffspring", {"start": v(26.75, 22.45) * mm, "mid": v(26.26, 23.03) * mm, "end": v(25.75, 23.6) * mm});
            skArc(sketch, "E22.trimOffspring", {"start": v(31.65, 14.76) * mm, "mid": v(31.32, 15.45) * mm, "end": v(30.98, 16.12) * mm});
            skArc(sketch, "E23.trimOffspring", {"start": v(34.4, 6.07) * mm, "mid": v(34.25, 6.81) * mm, "end": v(34.1, 7.56) * mm});
            skArc(sketch, "E24.trimOffspring", {"start": v(-34.8, 3.04) * mm, "mid": v(-34.85, 2.28) * mm, "end": v(-34.9, 1.53) * mm});
            skArc(sketch, "E25.trimOffspring", {"start": v(-32.82, 11.94) * mm, "mid": v(-33.07, 11.23) * mm, "end": v(-33.3, 10.5) * mm});
            skArc(sketch, "E26.trimOffspring", {"start": v(-34.4, -6.07) * mm, "mid": v(-34.25, -6.81) * mm, "end": v(-34.1, -7.56) * mm});
            skArc(sketch, "E27.trimOffspring", {"start": v(-31.65, -14.76) * mm, "mid": v(-31.32, -15.45) * mm, "end": v(-30.98, -16.12) * mm});
            skArc(sketch, "E28.trimOffspring", {"start": v(-26.75, -22.45) * mm, "mid": v(-26.26, -23.03) * mm, "end": v(-25.75, -23.6) * mm});
            skArc(sketch, "E29.trimOffspring", {"start": v(-11.94, -32.82) * mm, "mid": v(-11.23, -33.07) * mm, "end": v(-10.5, -33.3) * mm});
            skArc(sketch, "E30.trimOffspring", {"start": v(-20.03, -28.61) * mm, "mid": v(-19.4, -29.04) * mm, "end": v(-18.77, -29.45) * mm});
            skArc(sketch, "E31.trimOffspring", {"start": v(-3.04, -34.8) * mm, "mid": v(-2.28, -34.85) * mm, "end": v(-1.53, -34.9) * mm});
            skArc(sketch, "E32.trimOffspring", {"start": v(6.07, -34.4) * mm, "mid": v(6.81, -34.25) * mm, "end": v(7.56, -34.1) * mm});
            skArc(sketch, "E33.trimOffspring", {"start": v(14.76, -31.65) * mm, "mid": v(15.45, -31.32) * mm, "end": v(16.12, -30.98) * mm});
            skArc(sketch, "E34.trimOffspring", {"start": v(22.45, -26.75) * mm, "mid": v(23.03, -26.26) * mm, "end": v(23.6, -25.75) * mm});
            skArc(sketch, "E35.trimOffspring", {"start": v(34.8, -3.04) * mm, "mid": v(34.85, -2.28) * mm, "end": v(34.9, -1.53) * mm});
            skArc(sketch, "E36.trimOffspring", {"start": v(32.82, -11.94) * mm, "mid": v(33.07, -11.23) * mm, "end": v(33.3, -10.5) * mm});
            skArc(sketch, "E37.trimOffspring", {"start": v(28.61, -20.03) * mm, "mid": v(29.04, -19.4) * mm, "end": v(29.45, -18.77) * mm});
            skSolve(sketch);
        }
        {
            var Q0;
            Q0=makeQuery(id+"F0.imprint","IMPRINT",FACE,{"disambiguationData":[TD([[makeQuery(id+"F0.imprint","IMPRINT",EDGE,{"derivedFrom":sQuery(id+"F0.wireOp",EDGE,"E0")}),1.0]])]});
            cPlane(context, id + "F1", {"entities" : qUnion([Q0]), "cplaneType" : CPlaneType.OFFSET, "offset" : 50.8 * mm, "width" : 152.4 * mm, "height" : 152.4 * mm});
        }
        {
            var Q0;
            Q0=qCreatedBy(id+"F1.planeOp",FACE);
            var sketch = newSketch(context, id + "F2", { "sketchPlane" : qUnion([Q0])});
            skArc(sketch, "E38.0.0", {"start": v(-38.1, -4.9) * mm, "mid": v(-37.79, -4.95) * mm, "end": v(-37.47, -4.94) * mm});
            skLineSegment(sketch, "E38.0.1", {"start": v(-37.47, -4.94) * mm, "end": v(-36.16, -4.77) * mm});
            skArc(sketch, "E38.0.2", {"start": v(-36.16, -4.77) * mm, "mid": v(-35.02, -5.06) * mm, "end": v(-34.4, -6.07) * mm});
            skArc(sketch, "E38.0.3", {"start": v(-34.4, -6.07) * mm, "mid": v(-34.25, -6.81) * mm, "end": v(-34.1, -7.56) * mm});
            skArc(sketch, "E38.0.4", {"start": v(-34.1, -7.56) * mm, "mid": v(-34.3, -8.72) * mm, "end": v(-35.24, -9.43) * mm});
            skLineSegment(sketch, "E38.0.5", {"start": v(-35.24, -9.43) * mm, "end": v(-36.5, -9.77) * mm});
            skArc(sketch, "E38.0.6", {"start": v(-36.5, -9.77) * mm, "mid": v(-36.8, -9.89) * mm, "end": v(-37.07, -10.06) * mm});
            skArc(sketch, "E38.0.7", {"start": v(-37.07, -10.06) * mm, "mid": v(-38.23, -11.13) * mm, "end": v(-39.2, -12.37) * mm});
            skArc(sketch, "E38.0.8", {"start": v(-39.2, -12.37) * mm, "mid": v(-39.27, -12.57) * mm, "end": v(-39.26, -12.78) * mm});
            skLineSegment(sketch, "E38.0.9", {"start": v(-39.26, -12.78) * mm, "end": v(-39.12, -13.28) * mm});
            skLineSegment(sketch, "E38.0.10", {"start": v(-39.12, -13.28) * mm, "end": v(-38.93, -13.76) * mm});
            skArc(sketch, "E38.0.11", {"start": v(-38.93, -13.76) * mm, "mid": v(-38.8, -13.93) * mm, "end": v(-38.63, -14.04) * mm});
            skArc(sketch, "E38.0.12", {"start": v(-38.63, -14.04) * mm, "mid": v(-37.1, -14.45) * mm, "end": v(-35.53, -14.6) * mm});
            skArc(sketch, "E38.0.13", {"start": v(-35.53, -14.6) * mm, "mid": v(-35.22, -14.56) * mm, "end": v(-34.91, -14.47) * mm});
            skLineSegment(sketch, "E38.0.14", {"start": v(-34.91, -14.47) * mm, "end": v(-33.7, -13.97) * mm});
            skArc(sketch, "E38.0.15", {"start": v(-33.7, -13.97) * mm, "mid": v(-32.51, -13.95) * mm, "end": v(-31.65, -14.76) * mm});
            skArc(sketch, "E38.0.16", {"start": v(-31.65, -14.76) * mm, "mid": v(-31.32, -15.45) * mm, "end": v(-30.98, -16.12) * mm});
            skArc(sketch, "E38.0.17", {"start": v(-30.98, -16.12) * mm, "mid": v(-30.86, -17.3) * mm, "end": v(-31.6, -18.23) * mm});
            skLineSegment(sketch, "E38.0.18", {"start": v(-31.6, -18.23) * mm, "end": v(-32.73, -18.89) * mm});
            skArc(sketch, "E38.0.19", {"start": v(-32.73, -18.89) * mm, "mid": v(-33, -19.07) * mm, "end": v(-33.2, -19.3) * mm});
            skArc(sketch, "E38.0.20", {"start": v(-33.2, -19.3) * mm, "mid": v(-34.05, -20.64) * mm, "end": v(-34.66, -22.1) * mm});
            skArc(sketch, "E38.0.21", {"start": v(-34.66, -22.1) * mm, "mid": v(-34.68, -22.3) * mm, "end": v(-34.61, -22.5) * mm});
            skLineSegment(sketch, "E38.0.22", {"start": v(-34.61, -22.5) * mm, "end": v(-34.35, -22.95) * mm});
            skLineSegment(sketch, "E38.0.23", {"start": v(-34.35, -22.95) * mm, "end": v(-34.04, -23.36) * mm});
            skArc(sketch, "E38.0.24", {"start": v(-34.04, -23.36) * mm, "mid": v(-33.88, -23.5) * mm, "end": v(-33.68, -23.56) * mm});
            skArc(sketch, "E38.0.25", {"start": v(-33.68, -23.56) * mm, "mid": v(-32.1, -23.56) * mm, "end": v(-30.55, -23.3) * mm});
            skArc(sketch, "E38.0.26", {"start": v(-30.55, -23.3) * mm, "mid": v(-30.25, -23.18) * mm, "end": v(-29.98, -23.01) * mm});
            skLineSegment(sketch, "E38.0.27", {"start": v(-29.98, -23.01) * mm, "end": v(-28.93, -22.21) * mm});
            skArc(sketch, "E38.0.28", {"start": v(-28.93, -22.21) * mm, "mid": v(-27.8, -21.9) * mm, "end": v(-26.75, -22.45) * mm});
            skArc(sketch, "E38.0.29", {"start": v(-26.75, -22.45) * mm, "mid": v(-26.26, -23.03) * mm, "end": v(-25.75, -23.6) * mm});
            skArc(sketch, "E38.0.30", {"start": v(-25.75, -23.6) * mm, "mid": v(-25.34, -24.7) * mm, "end": v(-25.8, -25.79) * mm});
            skLineSegment(sketch, "E38.0.31", {"start": v(-25.8, -25.79) * mm, "end": v(-26.73, -26.72) * mm});
            skArc(sketch, "E38.0.32", {"start": v(-26.73, -26.72) * mm, "mid": v(-26.93, -26.96) * mm, "end": v(-27.08, -27.25) * mm});
            skArc(sketch, "E38.0.33", {"start": v(-27.08, -27.25) * mm, "mid": v(-27.54, -28.75) * mm, "end": v(-27.76, -30.31) * mm});
            skArc(sketch, "E38.0.34", {"start": v(-27.76, -30.31) * mm, "mid": v(-27.72, -30.52) * mm, "end": v(-27.6, -30.7) * mm});
            skLineSegment(sketch, "E38.0.35", {"start": v(-27.6, -30.7) * mm, "end": v(-27.24, -31.06) * mm});
            skLineSegment(sketch, "E38.0.36", {"start": v(-27.24, -31.06) * mm, "end": v(-26.83, -31.38) * mm});
            skArc(sketch, "E38.0.37", {"start": v(-26.83, -31.38) * mm, "mid": v(-26.64, -31.47) * mm, "end": v(-26.43, -31.48) * mm});
            skArc(sketch, "E38.0.38", {"start": v(-26.43, -31.48) * mm, "mid": v(-24.9, -31.06) * mm, "end": v(-23.48, -30.4) * mm});
            skArc(sketch, "E38.0.39", {"start": v(-23.48, -30.4) * mm, "mid": v(-23.22, -30.22) * mm, "end": v(-23, -29.99) * mm});
            skLineSegment(sketch, "E38.0.40", {"start": v(-23, -29.99) * mm, "end": v(-22.2, -28.94) * mm});
            skArc(sketch, "E38.0.41", {"start": v(-22.2, -28.94) * mm, "mid": v(-21.18, -28.34) * mm, "end": v(-20.03, -28.61) * mm});
            skArc(sketch, "E38.0.42", {"start": v(-20.03, -28.61) * mm, "mid": v(-19.4, -29.04) * mm, "end": v(-18.77, -29.45) * mm});
            skArc(sketch, "E38.0.43", {"start": v(-18.77, -29.45) * mm, "mid": v(-18.08, -30.42) * mm, "end": v(-18.25, -31.59) * mm});
            skLineSegment(sketch, "E38.0.44", {"start": v(-18.25, -31.59) * mm, "end": v(-18.9, -32.72) * mm});
            skArc(sketch, "E38.0.45", {"start": v(-18.9, -32.72) * mm, "mid": v(-19.03, -33.01) * mm, "end": v(-19.1, -33.33) * mm});
            skArc(sketch, "E38.0.46", {"start": v(-19.1, -33.33) * mm, "mid": v(-19.16, -34.9) * mm, "end": v(-18.96, -36.46) * mm});
            skArc(sketch, "E38.0.47", {"start": v(-18.96, -36.46) * mm, "mid": v(-18.88, -36.66) * mm, "end": v(-18.72, -36.8) * mm});
            skLineSegment(sketch, "E38.0.48", {"start": v(-18.72, -36.8) * mm, "end": v(-18.27, -37.06) * mm});
            skLineSegment(sketch, "E38.0.49", {"start": v(-18.27, -37.06) * mm, "end": v(-17.8, -37.25) * mm});
            skArc(sketch, "E38.0.50", {"start": v(-17.8, -37.25) * mm, "mid": v(-17.59, -37.3) * mm, "end": v(-17.38, -37.24) * mm});
            skArc(sketch, "E38.0.51", {"start": v(-17.38, -37.24) * mm, "mid": v(-16.02, -36.45) * mm, "end": v(-14.8, -35.44) * mm});
            skArc(sketch, "E38.0.52", {"start": v(-14.8, -35.44) * mm, "mid": v(-14.6, -35.2) * mm, "end": v(-14.45, -34.92) * mm});
            skLineSegment(sketch, "E38.0.53", {"start": v(-14.45, -34.92) * mm, "end": v(-13.95, -33.7) * mm});
            skArc(sketch, "E38.0.54", {"start": v(-13.95, -33.7) * mm, "mid": v(-13.12, -32.86) * mm, "end": v(-11.94, -32.82) * mm});
            skArc(sketch, "E38.0.55", {"start": v(-11.94, -32.82) * mm, "mid": v(-11.23, -33.07) * mm, "end": v(-10.5, -33.3) * mm});
            skArc(sketch, "E38.0.56", {"start": v(-10.5, -33.3) * mm, "mid": v(-9.6, -34.06) * mm, "end": v(-9.45, -35.23) * mm});
            skLineSegment(sketch, "E38.0.57", {"start": v(-9.45, -35.23) * mm, "end": v(-9.79, -36.5) * mm});
            skArc(sketch, "E38.0.58", {"start": v(-9.79, -36.5) * mm, "mid": v(-9.84, -36.82) * mm, "end": v(-9.83, -37.13) * mm});
            skArc(sketch, "E38.0.59", {"start": v(-9.83, -37.13) * mm, "mid": v(-9.48, -38.67) * mm, "end": v(-8.88, -40.13) * mm});
            skArc(sketch, "E38.0.60", {"start": v(-8.88, -40.13) * mm, "mid": v(-8.75, -40.3) * mm, "end": v(-8.56, -40.39) * mm});
            skLineSegment(sketch, "E38.0.61", {"start": v(-8.56, -40.39) * mm, "end": v(-8.06, -40.52) * mm});
            skLineSegment(sketch, "E38.0.62", {"start": v(-8.06, -40.52) * mm, "end": v(-7.55, -40.6) * mm});
            skArc(sketch, "E38.0.63", {"start": v(-7.55, -40.6) * mm, "mid": v(-7.34, -40.57) * mm, "end": v(-7.15, -40.47) * mm});
            skArc(sketch, "E38.0.64", {"start": v(-7.15, -40.47) * mm, "mid": v(-6.04, -39.36) * mm, "end": v(-5.13, -38.07) * mm});
            skArc(sketch, "E38.0.65", {"start": v(-5.13, -38.07) * mm, "mid": v(-5, -37.78) * mm, "end": v(-4.92, -37.47) * mm});
            skLineSegment(sketch, "E38.0.66", {"start": v(-4.92, -37.47) * mm, "end": v(-4.75, -36.17) * mm});
            skArc(sketch, "E38.0.67", {"start": v(-4.75, -36.17) * mm, "mid": v(-4.17, -35.14) * mm, "end": v(-3.04, -34.8) * mm});
            skArc(sketch, "E38.0.68", {"start": v(-3.04, -34.8) * mm, "mid": v(-2.28, -34.85) * mm, "end": v(-1.53, -34.9) * mm});
            skArc(sketch, "E38.0.69", {"start": v(-1.53, -34.9) * mm, "mid": v(-0.45, -35.38) * mm, "end": v(0, -36.48) * mm});
            skLineSegment(sketch, "E38.0.70", {"start": v(0, -36.48) * mm, "end": v(0, -37.8) * mm});
            skArc(sketch, "E38.0.71", {"start": v(0, -37.8) * mm, "mid": v(0.02, -38.1) * mm, "end": v(0.12, -38.41) * mm});
            skArc(sketch, "E38.0.72", {"start": v(0.12, -38.41) * mm, "mid": v(0.85, -39.8) * mm, "end": v(1.8, -41.06) * mm});
            skArc(sketch, "E38.0.73", {"start": v(1.8, -41.06) * mm, "mid": v(1.98, -41.18) * mm, "end": v(2.18, -41.23) * mm});
            skLineSegment(sketch, "E38.0.74", {"start": v(2.18, -41.23) * mm, "end": v(2.7, -41.23) * mm});
            skLineSegment(sketch, "E38.0.75", {"start": v(2.7, -41.23) * mm, "end": v(3.22, -41.16) * mm});
            skArc(sketch, "E38.0.76", {"start": v(3.22, -41.16) * mm, "mid": v(3.41, -41.1) * mm, "end": v(3.57, -40.95) * mm});
            skArc(sketch, "E38.0.77", {"start": v(3.57, -40.95) * mm, "mid": v(4.35, -39.58) * mm, "end": v(4.9, -38.1) * mm});
            skArc(sketch, "E38.0.78", {"start": v(4.9, -38.1) * mm, "mid": v(4.95, -37.79) * mm, "end": v(4.94, -37.47) * mm});
            skLineSegment(sketch, "E38.0.79", {"start": v(4.94, -37.47) * mm, "end": v(4.77, -36.16) * mm});
            skArc(sketch, "E38.0.80", {"start": v(4.77, -36.16) * mm, "mid": v(5.06, -35.02) * mm, "end": v(6.07, -34.4) * mm});
            skArc(sketch, "E38.0.81", {"start": v(6.07, -34.4) * mm, "mid": v(6.81, -34.25) * mm, "end": v(7.56, -34.1) * mm});
            skArc(sketch, "E38.0.82", {"start": v(7.56, -34.1) * mm, "mid": v(8.72, -34.3) * mm, "end": v(9.43, -35.24) * mm});
            skLineSegment(sketch, "E38.0.83", {"start": v(9.43, -35.24) * mm, "end": v(9.77, -36.5) * mm});
            skArc(sketch, "E38.0.84", {"start": v(9.77, -36.5) * mm, "mid": v(9.89, -36.8) * mm, "end": v(10.06, -37.07) * mm});
            skArc(sketch, "E38.0.85", {"start": v(10.06, -37.07) * mm, "mid": v(11.13, -38.23) * mm, "end": v(12.37, -39.2) * mm});
            skArc(sketch, "E38.0.86", {"start": v(12.37, -39.2) * mm, "mid": v(12.57, -39.27) * mm, "end": v(12.78, -39.26) * mm});
            skLineSegment(sketch, "E38.0.87", {"start": v(12.78, -39.26) * mm, "end": v(13.28, -39.12) * mm});
            skLineSegment(sketch, "E38.0.88", {"start": v(13.28, -39.12) * mm, "end": v(13.76, -38.93) * mm});
            skArc(sketch, "E38.0.89", {"start": v(13.76, -38.93) * mm, "mid": v(13.93, -38.8) * mm, "end": v(14.04, -38.63) * mm});
            skArc(sketch, "E38.0.90", {"start": v(14.04, -38.63) * mm, "mid": v(14.45, -37.1) * mm, "end": v(14.6, -35.53) * mm});
            skArc(sketch, "E38.0.91", {"start": v(14.6, -35.53) * mm, "mid": v(14.56, -35.22) * mm, "end": v(14.47, -34.91) * mm});
            skLineSegment(sketch, "E38.0.92", {"start": v(14.47, -34.91) * mm, "end": v(13.97, -33.7) * mm});
            skArc(sketch, "E38.0.93", {"start": v(13.97, -33.7) * mm, "mid": v(13.95, -32.51) * mm, "end": v(14.76, -31.65) * mm});
            skArc(sketch, "E38.0.94", {"start": v(14.76, -31.65) * mm, "mid": v(15.45, -31.32) * mm, "end": v(16.12, -30.98) * mm});
            skArc(sketch, "E38.0.95", {"start": v(16.12, -30.98) * mm, "mid": v(17.3, -30.86) * mm, "end": v(18.23, -31.6) * mm});
            skLineSegment(sketch, "E38.0.96", {"start": v(18.23, -31.6) * mm, "end": v(18.89, -32.73) * mm});
            skArc(sketch, "E38.0.97", {"start": v(18.89, -32.73) * mm, "mid": v(19.07, -33) * mm, "end": v(19.3, -33.2) * mm});
            skArc(sketch, "E38.0.98", {"start": v(19.3, -33.2) * mm, "mid": v(20.64, -34.05) * mm, "end": v(22.1, -34.66) * mm});
            skArc(sketch, "E38.0.99", {"start": v(22.1, -34.66) * mm, "mid": v(22.3, -34.68) * mm, "end": v(22.5, -34.61) * mm});
            skLineSegment(sketch, "E38.0.100", {"start": v(22.5, -34.61) * mm, "end": v(22.95, -34.35) * mm});
            skLineSegment(sketch, "E38.0.101", {"start": v(22.95, -34.35) * mm, "end": v(23.36, -34.04) * mm});
            skArc(sketch, "E38.0.102", {"start": v(23.36, -34.04) * mm, "mid": v(23.5, -33.88) * mm, "end": v(23.56, -33.68) * mm});
            skArc(sketch, "E38.0.103", {"start": v(23.56, -33.68) * mm, "mid": v(23.56, -32.1) * mm, "end": v(23.3, -30.55) * mm});
            skArc(sketch, "E38.0.104", {"start": v(23.3, -30.55) * mm, "mid": v(23.18, -30.25) * mm, "end": v(23.01, -29.98) * mm});
            skLineSegment(sketch, "E38.0.105", {"start": v(23.01, -29.98) * mm, "end": v(22.21, -28.93) * mm});
            skArc(sketch, "E38.0.106", {"start": v(22.21, -28.93) * mm, "mid": v(21.9, -27.8) * mm, "end": v(22.45, -26.75) * mm});
            skArc(sketch, "E38.0.107", {"start": v(22.45, -26.75) * mm, "mid": v(23.03, -26.26) * mm, "end": v(23.6, -25.75) * mm});
            skArc(sketch, "E38.0.108", {"start": v(23.6, -25.75) * mm, "mid": v(24.7, -25.34) * mm, "end": v(25.79, -25.8) * mm});
            skLineSegment(sketch, "E38.0.109", {"start": v(25.79, -25.8) * mm, "end": v(26.72, -26.73) * mm});
            skArc(sketch, "E38.0.110", {"start": v(26.72, -26.73) * mm, "mid": v(26.96, -26.93) * mm, "end": v(27.25, -27.08) * mm});
            skArc(sketch, "E38.0.111", {"start": v(27.25, -27.08) * mm, "mid": v(28.75, -27.54) * mm, "end": v(30.31, -27.76) * mm});
            skArc(sketch, "E38.0.112", {"start": v(30.31, -27.76) * mm, "mid": v(30.52, -27.72) * mm, "end": v(30.7, -27.6) * mm});
            skLineSegment(sketch, "E38.0.113", {"start": v(30.7, -27.6) * mm, "end": v(31.06, -27.24) * mm});
            skLineSegment(sketch, "E38.0.114", {"start": v(31.06, -27.24) * mm, "end": v(31.38, -26.83) * mm});
            skArc(sketch, "E38.0.115", {"start": v(31.38, -26.83) * mm, "mid": v(31.47, -26.64) * mm, "end": v(31.48, -26.43) * mm});
            skArc(sketch, "E38.0.116", {"start": v(31.48, -26.43) * mm, "mid": v(31.06, -24.9) * mm, "end": v(30.4, -23.48) * mm});
            skArc(sketch, "E38.0.117", {"start": v(30.4, -23.48) * mm, "mid": v(30.22, -23.22) * mm, "end": v(29.99, -23) * mm});
            skLineSegment(sketch, "E38.0.118", {"start": v(29.99, -23) * mm, "end": v(28.94, -22.2) * mm});
            skArc(sketch, "E38.0.119", {"start": v(28.94, -22.2) * mm, "mid": v(28.34, -21.18) * mm, "end": v(28.61, -20.03) * mm});
            skArc(sketch, "E38.0.120", {"start": v(28.61, -20.03) * mm, "mid": v(29.04, -19.4) * mm, "end": v(29.45, -18.77) * mm});
            skArc(sketch, "E38.0.121", {"start": v(29.45, -18.77) * mm, "mid": v(30.42, -18.08) * mm, "end": v(31.59, -18.25) * mm});
            skLineSegment(sketch, "E38.0.122", {"start": v(31.59, -18.25) * mm, "end": v(32.72, -18.9) * mm});
            skArc(sketch, "E38.0.123", {"start": v(32.72, -18.9) * mm, "mid": v(33.01, -19.03) * mm, "end": v(33.33, -19.1) * mm});
            skArc(sketch, "E38.0.124", {"start": v(33.33, -19.1) * mm, "mid": v(34.9, -19.16) * mm, "end": v(36.46, -18.96) * mm});
            skArc(sketch, "E38.0.125", {"start": v(36.46, -18.96) * mm, "mid": v(36.66, -18.88) * mm, "end": v(36.8, -18.72) * mm});
            skLineSegment(sketch, "E38.0.126", {"start": v(36.8, -18.72) * mm, "end": v(37.06, -18.27) * mm});
            skLineSegment(sketch, "E38.0.127", {"start": v(37.06, -18.27) * mm, "end": v(37.25, -17.8) * mm});
            skArc(sketch, "E38.0.128", {"start": v(37.25, -17.8) * mm, "mid": v(37.3, -17.59) * mm, "end": v(37.24, -17.38) * mm});
            skArc(sketch, "E38.0.129", {"start": v(37.24, -17.38) * mm, "mid": v(36.45, -16.02) * mm, "end": v(35.44, -14.8) * mm});
            skArc(sketch, "E38.0.130", {"start": v(35.44, -14.8) * mm, "mid": v(35.2, -14.6) * mm, "end": v(34.92, -14.45) * mm});
            skLineSegment(sketch, "E38.0.131", {"start": v(34.92, -14.45) * mm, "end": v(33.7, -13.95) * mm});
            skArc(sketch, "E38.0.132", {"start": v(33.7, -13.95) * mm, "mid": v(32.86, -13.12) * mm, "end": v(32.82, -11.94) * mm});
            skArc(sketch, "E38.0.133", {"start": v(32.82, -11.94) * mm, "mid": v(33.07, -11.23) * mm, "end": v(33.3, -10.5) * mm});
            skArc(sketch, "E38.0.134", {"start": v(33.3, -10.5) * mm, "mid": v(34.06, -9.6) * mm, "end": v(35.23, -9.45) * mm});
            skLineSegment(sketch, "E38.0.135", {"start": v(35.23, -9.45) * mm, "end": v(36.5, -9.79) * mm});
            skArc(sketch, "E38.0.136", {"start": v(36.5, -9.79) * mm, "mid": v(36.82, -9.84) * mm, "end": v(37.13, -9.83) * mm});
            skArc(sketch, "E38.0.137", {"start": v(37.13, -9.83) * mm, "mid": v(38.67, -9.48) * mm, "end": v(40.13, -8.88) * mm});
            skArc(sketch, "E38.0.138", {"start": v(40.13, -8.88) * mm, "mid": v(40.3, -8.75) * mm, "end": v(40.39, -8.56) * mm});
            skLineSegment(sketch, "E38.0.139", {"start": v(40.39, -8.56) * mm, "end": v(40.52, -8.06) * mm});
            skLineSegment(sketch, "E38.0.140", {"start": v(40.52, -8.06) * mm, "end": v(40.6, -7.55) * mm});
            skArc(sketch, "E38.0.141", {"start": v(40.6, -7.55) * mm, "mid": v(40.57, -7.34) * mm, "end": v(40.47, -7.15) * mm});
            skArc(sketch, "E38.0.142", {"start": v(40.47, -7.15) * mm, "mid": v(39.36, -6.04) * mm, "end": v(38.07, -5.13) * mm});
            skArc(sketch, "E38.0.143", {"start": v(38.07, -5.13) * mm, "mid": v(37.78, -5) * mm, "end": v(37.47, -4.92) * mm});
            skLineSegment(sketch, "E38.0.144", {"start": v(37.47, -4.92) * mm, "end": v(36.17, -4.75) * mm});
            skArc(sketch, "E38.0.145", {"start": v(36.17, -4.75) * mm, "mid": v(35.14, -4.17) * mm, "end": v(34.8, -3.04) * mm});
            skArc(sketch, "E38.0.146", {"start": v(34.8, -3.04) * mm, "mid": v(34.85, -2.28) * mm, "end": v(34.9, -1.53) * mm});
            skArc(sketch, "E38.0.147", {"start": v(34.9, -1.53) * mm, "mid": v(35.38, -0.45) * mm, "end": v(36.48, 0) * mm});
            skLineSegment(sketch, "E38.0.148", {"start": v(36.48, 0) * mm, "end": v(37.8, 0) * mm});
            skArc(sketch, "E38.0.149", {"start": v(37.8, 0) * mm, "mid": v(38.1, 0.02) * mm, "end": v(38.41, 0.12) * mm});
            skArc(sketch, "E38.0.150", {"start": v(38.41, 0.12) * mm, "mid": v(39.8, 0.85) * mm, "end": v(41.06, 1.8) * mm});
            skArc(sketch, "E38.0.151", {"start": v(41.06, 1.8) * mm, "mid": v(41.18, 1.98) * mm, "end": v(41.23, 2.18) * mm});
            skLineSegment(sketch, "E38.0.152", {"start": v(41.23, 2.18) * mm, "end": v(41.23, 2.7) * mm});
            skLineSegment(sketch, "E38.0.153", {"start": v(41.23, 2.7) * mm, "end": v(41.16, 3.22) * mm});
            skArc(sketch, "E38.0.154", {"start": v(41.16, 3.22) * mm, "mid": v(41.1, 3.41) * mm, "end": v(40.95, 3.57) * mm});
            skArc(sketch, "E38.0.155", {"start": v(40.95, 3.57) * mm, "mid": v(39.58, 4.35) * mm, "end": v(38.1, 4.9) * mm});
            skArc(sketch, "E38.0.156", {"start": v(38.1, 4.9) * mm, "mid": v(37.79, 4.95) * mm, "end": v(37.47, 4.94) * mm});
            skLineSegment(sketch, "E38.0.157", {"start": v(37.47, 4.94) * mm, "end": v(36.16, 4.77) * mm});
            skArc(sketch, "E38.0.158", {"start": v(36.16, 4.77) * mm, "mid": v(35.02, 5.06) * mm, "end": v(34.4, 6.07) * mm});
            skArc(sketch, "E38.0.159", {"start": v(34.4, 6.07) * mm, "mid": v(34.25, 6.81) * mm, "end": v(34.1, 7.56) * mm});
            skArc(sketch, "E38.0.160", {"start": v(34.1, 7.56) * mm, "mid": v(34.3, 8.72) * mm, "end": v(35.24, 9.43) * mm});
            skLineSegment(sketch, "E38.0.161", {"start": v(35.24, 9.43) * mm, "end": v(36.5, 9.77) * mm});
            skArc(sketch, "E38.0.162", {"start": v(36.5, 9.77) * mm, "mid": v(36.8, 9.89) * mm, "end": v(37.07, 10.06) * mm});
            skArc(sketch, "E38.0.163", {"start": v(37.07, 10.06) * mm, "mid": v(38.23, 11.13) * mm, "end": v(39.2, 12.37) * mm});
            skArc(sketch, "E38.0.164", {"start": v(39.2, 12.37) * mm, "mid": v(39.27, 12.57) * mm, "end": v(39.26, 12.78) * mm});
            skLineSegment(sketch, "E38.0.165", {"start": v(39.26, 12.78) * mm, "end": v(39.12, 13.28) * mm});
            skLineSegment(sketch, "E38.0.166", {"start": v(39.12, 13.28) * mm, "end": v(38.93, 13.76) * mm});
            skArc(sketch, "E38.0.167", {"start": v(38.93, 13.76) * mm, "mid": v(38.8, 13.93) * mm, "end": v(38.63, 14.04) * mm});
            skArc(sketch, "E38.0.168", {"start": v(38.63, 14.04) * mm, "mid": v(37.1, 14.45) * mm, "end": v(35.53, 14.6) * mm});
            skArc(sketch, "E38.0.169", {"start": v(35.53, 14.6) * mm, "mid": v(35.22, 14.56) * mm, "end": v(34.91, 14.47) * mm});
            skLineSegment(sketch, "E38.0.170", {"start": v(34.91, 14.47) * mm, "end": v(33.7, 13.97) * mm});
            skArc(sketch, "E38.0.171", {"start": v(33.7, 13.97) * mm, "mid": v(32.51, 13.95) * mm, "end": v(31.65, 14.76) * mm});
            skArc(sketch, "E38.0.172", {"start": v(31.65, 14.76) * mm, "mid": v(31.32, 15.45) * mm, "end": v(30.98, 16.12) * mm});
            skArc(sketch, "E38.0.173", {"start": v(30.98, 16.12) * mm, "mid": v(30.86, 17.3) * mm, "end": v(31.6, 18.23) * mm});
            skLineSegment(sketch, "E38.0.174", {"start": v(31.6, 18.23) * mm, "end": v(32.73, 18.89) * mm});
            skArc(sketch, "E38.0.175", {"start": v(32.73, 18.89) * mm, "mid": v(33, 19.07) * mm, "end": v(33.2, 19.3) * mm});
            skArc(sketch, "E38.0.176", {"start": v(33.2, 19.3) * mm, "mid": v(34.05, 20.64) * mm, "end": v(34.66, 22.1) * mm});
            skArc(sketch, "E38.0.177", {"start": v(34.66, 22.1) * mm, "mid": v(34.68, 22.3) * mm, "end": v(34.61, 22.5) * mm});
            skLineSegment(sketch, "E38.0.178", {"start": v(34.61, 22.5) * mm, "end": v(34.35, 22.95) * mm});
            skLineSegment(sketch, "E38.0.179", {"start": v(34.35, 22.95) * mm, "end": v(34.04, 23.36) * mm});
            skArc(sketch, "E38.0.180", {"start": v(34.04, 23.36) * mm, "mid": v(33.88, 23.5) * mm, "end": v(33.68, 23.56) * mm});
            skArc(sketch, "E38.0.181", {"start": v(33.68, 23.56) * mm, "mid": v(32.1, 23.56) * mm, "end": v(30.55, 23.3) * mm});
            skArc(sketch, "E38.0.182", {"start": v(30.55, 23.3) * mm, "mid": v(30.25, 23.18) * mm, "end": v(29.98, 23.01) * mm});
            skLineSegment(sketch, "E38.0.183", {"start": v(29.98, 23.01) * mm, "end": v(28.93, 22.21) * mm});
            skArc(sketch, "E38.0.184", {"start": v(28.93, 22.21) * mm, "mid": v(27.8, 21.9) * mm, "end": v(26.75, 22.45) * mm});
            skArc(sketch, "E38.0.185", {"start": v(26.75, 22.45) * mm, "mid": v(26.26, 23.03) * mm, "end": v(25.75, 23.6) * mm});
            skArc(sketch, "E38.0.186", {"start": v(25.75, 23.6) * mm, "mid": v(25.34, 24.7) * mm, "end": v(25.8, 25.79) * mm});
            skLineSegment(sketch, "E38.0.187", {"start": v(25.8, 25.79) * mm, "end": v(26.73, 26.72) * mm});
            skArc(sketch, "E38.0.188", {"start": v(26.73, 26.72) * mm, "mid": v(26.93, 26.96) * mm, "end": v(27.08, 27.25) * mm});
            skArc(sketch, "E38.0.189", {"start": v(27.08, 27.25) * mm, "mid": v(27.54, 28.75) * mm, "end": v(27.76, 30.31) * mm});
            skArc(sketch, "E38.0.190", {"start": v(27.76, 30.31) * mm, "mid": v(27.72, 30.52) * mm, "end": v(27.6, 30.7) * mm});
            skLineSegment(sketch, "E38.0.191", {"start": v(27.6, 30.7) * mm, "end": v(27.24, 31.06) * mm});
            skLineSegment(sketch, "E38.0.192", {"start": v(27.24, 31.06) * mm, "end": v(26.83, 31.38) * mm});
            skArc(sketch, "E38.0.193", {"start": v(26.83, 31.38) * mm, "mid": v(26.64, 31.47) * mm, "end": v(26.43, 31.48) * mm});
            skArc(sketch, "E38.0.194", {"start": v(26.43, 31.48) * mm, "mid": v(24.9, 31.06) * mm, "end": v(23.48, 30.4) * mm});
            skArc(sketch, "E38.0.195", {"start": v(23.48, 30.4) * mm, "mid": v(23.22, 30.22) * mm, "end": v(23, 29.99) * mm});
            skLineSegment(sketch, "E38.0.196", {"start": v(23, 29.99) * mm, "end": v(22.2, 28.94) * mm});
            skArc(sketch, "E38.0.197", {"start": v(22.2, 28.94) * mm, "mid": v(21.18, 28.34) * mm, "end": v(20.03, 28.61) * mm});
            skArc(sketch, "E38.0.198", {"start": v(20.03, 28.61) * mm, "mid": v(19.4, 29.04) * mm, "end": v(18.77, 29.45) * mm});
            skArc(sketch, "E38.0.199", {"start": v(18.77, 29.45) * mm, "mid": v(18.08, 30.42) * mm, "end": v(18.25, 31.59) * mm});
            skLineSegment(sketch, "E38.0.200", {"start": v(18.25, 31.59) * mm, "end": v(18.9, 32.72) * mm});
            skArc(sketch, "E38.0.201", {"start": v(18.9, 32.72) * mm, "mid": v(19.03, 33.01) * mm, "end": v(19.1, 33.33) * mm});
            skArc(sketch, "E38.0.202", {"start": v(19.1, 33.33) * mm, "mid": v(19.16, 34.9) * mm, "end": v(18.96, 36.46) * mm});
            skArc(sketch, "E38.0.203", {"start": v(18.96, 36.46) * mm, "mid": v(18.88, 36.66) * mm, "end": v(18.72, 36.8) * mm});
            skLineSegment(sketch, "E38.0.204", {"start": v(18.72, 36.8) * mm, "end": v(18.27, 37.06) * mm});
            skLineSegment(sketch, "E38.0.205", {"start": v(18.27, 37.06) * mm, "end": v(17.8, 37.25) * mm});
            skArc(sketch, "E38.0.206", {"start": v(17.8, 37.25) * mm, "mid": v(17.59, 37.3) * mm, "end": v(17.38, 37.24) * mm});
            skArc(sketch, "E38.0.207", {"start": v(17.38, 37.24) * mm, "mid": v(16.02, 36.45) * mm, "end": v(14.8, 35.44) * mm});
            skArc(sketch, "E38.0.208", {"start": v(14.8, 35.44) * mm, "mid": v(14.6, 35.2) * mm, "end": v(14.45, 34.92) * mm});
            skLineSegment(sketch, "E38.0.209", {"start": v(14.45, 34.92) * mm, "end": v(13.95, 33.7) * mm});
            skArc(sketch, "E38.0.210", {"start": v(13.95, 33.7) * mm, "mid": v(13.12, 32.86) * mm, "end": v(11.94, 32.82) * mm});
            skArc(sketch, "E38.0.211", {"start": v(11.94, 32.82) * mm, "mid": v(11.23, 33.07) * mm, "end": v(10.5, 33.3) * mm});
            skArc(sketch, "E38.0.212", {"start": v(10.5, 33.3) * mm, "mid": v(9.6, 34.06) * mm, "end": v(9.45, 35.23) * mm});
            skLineSegment(sketch, "E38.0.213", {"start": v(9.45, 35.23) * mm, "end": v(9.79, 36.5) * mm});
            skArc(sketch, "E38.0.214", {"start": v(9.79, 36.5) * mm, "mid": v(9.84, 36.82) * mm, "end": v(9.83, 37.13) * mm});
            skArc(sketch, "E38.0.215", {"start": v(9.83, 37.13) * mm, "mid": v(9.48, 38.67) * mm, "end": v(8.88, 40.13) * mm});
            skArc(sketch, "E38.0.216", {"start": v(8.88, 40.13) * mm, "mid": v(8.75, 40.3) * mm, "end": v(8.56, 40.39) * mm});
            skLineSegment(sketch, "E38.0.217", {"start": v(8.56, 40.39) * mm, "end": v(8.06, 40.52) * mm});
            skLineSegment(sketch, "E38.0.218", {"start": v(8.06, 40.52) * mm, "end": v(7.55, 40.6) * mm});
            skArc(sketch, "E38.0.219", {"start": v(7.55, 40.6) * mm, "mid": v(7.34, 40.57) * mm, "end": v(7.15, 40.47) * mm});
            skArc(sketch, "E38.0.220", {"start": v(7.15, 40.47) * mm, "mid": v(6.04, 39.36) * mm, "end": v(5.13, 38.07) * mm});
            skArc(sketch, "E38.0.221", {"start": v(5.13, 38.07) * mm, "mid": v(5, 37.78) * mm, "end": v(4.92, 37.47) * mm});
            skLineSegment(sketch, "E38.0.222", {"start": v(4.92, 37.47) * mm, "end": v(4.75, 36.17) * mm});
            skArc(sketch, "E38.0.223", {"start": v(4.75, 36.17) * mm, "mid": v(4.17, 35.14) * mm, "end": v(3.04, 34.8) * mm});
            skArc(sketch, "E38.0.224", {"start": v(3.04, 34.8) * mm, "mid": v(2.28, 34.85) * mm, "end": v(1.53, 34.9) * mm});
            skArc(sketch, "E38.0.225", {"start": v(1.53, 34.9) * mm, "mid": v(0.45, 35.38) * mm, "end": v(0, 36.48) * mm});
            skLineSegment(sketch, "E38.0.226", {"start": v(0, 36.48) * mm, "end": v(0, 37.8) * mm});
            skArc(sketch, "E38.0.227", {"start": v(0, 37.8) * mm, "mid": v(-0.02, 38.1) * mm, "end": v(-0.12, 38.41) * mm});
            skArc(sketch, "E38.0.228", {"start": v(-0.12, 38.41) * mm, "mid": v(-0.85, 39.8) * mm, "end": v(-1.8, 41.06) * mm});
            skArc(sketch, "E38.0.229", {"start": v(-1.8, 41.06) * mm, "mid": v(-1.98, 41.18) * mm, "end": v(-2.18, 41.23) * mm});
            skLineSegment(sketch, "E38.0.230", {"start": v(-2.18, 41.23) * mm, "end": v(-2.7, 41.23) * mm});
            skLineSegment(sketch, "E38.0.231", {"start": v(-2.7, 41.23) * mm, "end": v(-3.22, 41.16) * mm});
            skArc(sketch, "E38.0.232", {"start": v(-3.22, 41.16) * mm, "mid": v(-3.41, 41.1) * mm, "end": v(-3.57, 40.95) * mm});
            skArc(sketch, "E38.0.233", {"start": v(-3.57, 40.95) * mm, "mid": v(-4.35, 39.58) * mm, "end": v(-4.9, 38.1) * mm});
            skArc(sketch, "E38.0.234", {"start": v(-4.9, 38.1) * mm, "mid": v(-4.95, 37.79) * mm, "end": v(-4.94, 37.47) * mm});
            skLineSegment(sketch, "E38.0.235", {"start": v(-4.94, 37.47) * mm, "end": v(-4.77, 36.16) * mm});
            skArc(sketch, "E38.0.236", {"start": v(-4.77, 36.16) * mm, "mid": v(-5.06, 35.02) * mm, "end": v(-6.07, 34.4) * mm});
            skArc(sketch, "E38.0.237", {"start": v(-6.07, 34.4) * mm, "mid": v(-6.81, 34.25) * mm, "end": v(-7.56, 34.1) * mm});
            skArc(sketch, "E38.0.238", {"start": v(-7.56, 34.1) * mm, "mid": v(-8.72, 34.3) * mm, "end": v(-9.43, 35.24) * mm});
            skLineSegment(sketch, "E38.0.239", {"start": v(-9.43, 35.24) * mm, "end": v(-9.77, 36.5) * mm});
            skArc(sketch, "E38.0.240", {"start": v(-9.77, 36.5) * mm, "mid": v(-9.89, 36.8) * mm, "end": v(-10.06, 37.07) * mm});
            skArc(sketch, "E38.0.241", {"start": v(-10.06, 37.07) * mm, "mid": v(-11.13, 38.23) * mm, "end": v(-12.37, 39.2) * mm});
            skArc(sketch, "E38.0.242", {"start": v(-12.37, 39.2) * mm, "mid": v(-12.57, 39.27) * mm, "end": v(-12.78, 39.26) * mm});
            skLineSegment(sketch, "E38.0.243", {"start": v(-12.78, 39.26) * mm, "end": v(-13.28, 39.12) * mm});
            skLineSegment(sketch, "E38.0.244", {"start": v(-13.28, 39.12) * mm, "end": v(-13.76, 38.93) * mm});
            skArc(sketch, "E38.0.245", {"start": v(-13.76, 38.93) * mm, "mid": v(-13.93, 38.8) * mm, "end": v(-14.04, 38.63) * mm});
            skArc(sketch, "E38.0.246", {"start": v(-14.04, 38.63) * mm, "mid": v(-14.45, 37.1) * mm, "end": v(-14.6, 35.53) * mm});
            skArc(sketch, "E38.0.247", {"start": v(-14.6, 35.53) * mm, "mid": v(-14.56, 35.22) * mm, "end": v(-14.47, 34.91) * mm});
            skLineSegment(sketch, "E38.0.248", {"start": v(-14.47, 34.91) * mm, "end": v(-13.97, 33.7) * mm});
            skArc(sketch, "E38.0.249", {"start": v(-13.97, 33.7) * mm, "mid": v(-13.95, 32.51) * mm, "end": v(-14.76, 31.65) * mm});
            skArc(sketch, "E38.0.250", {"start": v(-14.76, 31.65) * mm, "mid": v(-15.45, 31.32) * mm, "end": v(-16.12, 30.98) * mm});
            skArc(sketch, "E38.0.251", {"start": v(-16.12, 30.98) * mm, "mid": v(-17.3, 30.86) * mm, "end": v(-18.23, 31.6) * mm});
            skLineSegment(sketch, "E38.0.252", {"start": v(-18.23, 31.6) * mm, "end": v(-18.89, 32.73) * mm});
            skArc(sketch, "E38.0.253", {"start": v(-18.89, 32.73) * mm, "mid": v(-19.07, 33) * mm, "end": v(-19.3, 33.2) * mm});
            skArc(sketch, "E38.0.254", {"start": v(-19.3, 33.2) * mm, "mid": v(-20.64, 34.05) * mm, "end": v(-22.1, 34.66) * mm});
            skArc(sketch, "E38.0.255", {"start": v(-22.1, 34.66) * mm, "mid": v(-22.3, 34.68) * mm, "end": v(-22.5, 34.61) * mm});
            skLineSegment(sketch, "E38.0.256", {"start": v(-22.5, 34.61) * mm, "end": v(-22.95, 34.35) * mm});
            skLineSegment(sketch, "E38.0.257", {"start": v(-22.95, 34.35) * mm, "end": v(-23.36, 34.04) * mm});
            skArc(sketch, "E38.0.258", {"start": v(-23.36, 34.04) * mm, "mid": v(-23.5, 33.88) * mm, "end": v(-23.56, 33.68) * mm});
            skArc(sketch, "E38.0.259", {"start": v(-23.56, 33.68) * mm, "mid": v(-23.56, 32.1) * mm, "end": v(-23.3, 30.55) * mm});
            skArc(sketch, "E38.0.260", {"start": v(-23.3, 30.55) * mm, "mid": v(-23.18, 30.25) * mm, "end": v(-23.01, 29.98) * mm});
            skLineSegment(sketch, "E38.0.261", {"start": v(-23.01, 29.98) * mm, "end": v(-22.21, 28.93) * mm});
            skArc(sketch, "E38.0.262", {"start": v(-22.21, 28.93) * mm, "mid": v(-21.9, 27.8) * mm, "end": v(-22.45, 26.75) * mm});
            skArc(sketch, "E38.0.263", {"start": v(-22.45, 26.75) * mm, "mid": v(-23.03, 26.26) * mm, "end": v(-23.6, 25.75) * mm});
            skArc(sketch, "E38.0.264", {"start": v(-23.6, 25.75) * mm, "mid": v(-24.7, 25.34) * mm, "end": v(-25.79, 25.8) * mm});
            skLineSegment(sketch, "E38.0.265", {"start": v(-25.79, 25.8) * mm, "end": v(-26.72, 26.73) * mm});
            skArc(sketch, "E38.0.266", {"start": v(-26.72, 26.73) * mm, "mid": v(-26.96, 26.93) * mm, "end": v(-27.25, 27.08) * mm});
            skArc(sketch, "E38.0.267", {"start": v(-27.25, 27.08) * mm, "mid": v(-28.75, 27.54) * mm, "end": v(-30.31, 27.76) * mm});
            skArc(sketch, "E38.0.268", {"start": v(-30.31, 27.76) * mm, "mid": v(-30.52, 27.72) * mm, "end": v(-30.7, 27.6) * mm});
            skLineSegment(sketch, "E38.0.269", {"start": v(-30.7, 27.6) * mm, "end": v(-31.06, 27.24) * mm});
            skLineSegment(sketch, "E38.0.270", {"start": v(-31.06, 27.24) * mm, "end": v(-31.38, 26.83) * mm});
            skArc(sketch, "E38.0.271", {"start": v(-31.38, 26.83) * mm, "mid": v(-31.47, 26.64) * mm, "end": v(-31.48, 26.43) * mm});
            skArc(sketch, "E38.0.272", {"start": v(-31.48, 26.43) * mm, "mid": v(-31.06, 24.9) * mm, "end": v(-30.4, 23.48) * mm});
            skArc(sketch, "E38.0.273", {"start": v(-30.4, 23.48) * mm, "mid": v(-30.22, 23.22) * mm, "end": v(-29.99, 23) * mm});
            skLineSegment(sketch, "E38.0.274", {"start": v(-29.99, 23) * mm, "end": v(-28.94, 22.2) * mm});
            skArc(sketch, "E38.0.275", {"start": v(-28.94, 22.2) * mm, "mid": v(-28.34, 21.18) * mm, "end": v(-28.61, 20.03) * mm});
            skArc(sketch, "E38.0.276", {"start": v(-28.61, 20.03) * mm, "mid": v(-29.04, 19.4) * mm, "end": v(-29.45, 18.77) * mm});
            skArc(sketch, "E38.0.277", {"start": v(-29.45, 18.77) * mm, "mid": v(-30.42, 18.08) * mm, "end": v(-31.59, 18.25) * mm});
            skLineSegment(sketch, "E38.0.278", {"start": v(-31.59, 18.25) * mm, "end": v(-32.72, 18.9) * mm});
            skArc(sketch, "E38.0.279", {"start": v(-32.72, 18.9) * mm, "mid": v(-33.01, 19.03) * mm, "end": v(-33.33, 19.1) * mm});
            skArc(sketch, "E38.0.280", {"start": v(-33.33, 19.1) * mm, "mid": v(-34.9, 19.16) * mm, "end": v(-36.46, 18.96) * mm});
            skArc(sketch, "E38.0.281", {"start": v(-36.46, 18.96) * mm, "mid": v(-36.66, 18.88) * mm, "end": v(-36.8, 18.72) * mm});
            skLineSegment(sketch, "E38.0.282", {"start": v(-36.8, 18.72) * mm, "end": v(-37.06, 18.27) * mm});
            skLineSegment(sketch, "E38.0.283", {"start": v(-37.06, 18.27) * mm, "end": v(-37.25, 17.8) * mm});
            skArc(sketch, "E38.0.284", {"start": v(-37.25, 17.8) * mm, "mid": v(-37.3, 17.59) * mm, "end": v(-37.24, 17.38) * mm});
            skArc(sketch, "E38.0.285", {"start": v(-37.24, 17.38) * mm, "mid": v(-36.45, 16.02) * mm, "end": v(-35.44, 14.8) * mm});
            skArc(sketch, "E38.0.286", {"start": v(-35.44, 14.8) * mm, "mid": v(-35.2, 14.6) * mm, "end": v(-34.92, 14.45) * mm});
            skLineSegment(sketch, "E38.0.287", {"start": v(-34.92, 14.45) * mm, "end": v(-33.7, 13.95) * mm});
            skArc(sketch, "E38.0.288", {"start": v(-33.7, 13.95) * mm, "mid": v(-32.86, 13.12) * mm, "end": v(-32.82, 11.94) * mm});
            skArc(sketch, "E38.0.289", {"start": v(-32.82, 11.94) * mm, "mid": v(-33.07, 11.23) * mm, "end": v(-33.3, 10.5) * mm});
            skArc(sketch, "E38.0.290", {"start": v(-33.3, 10.5) * mm, "mid": v(-34.06, 9.6) * mm, "end": v(-35.23, 9.45) * mm});
            skLineSegment(sketch, "E38.0.291", {"start": v(-35.23, 9.45) * mm, "end": v(-36.5, 9.79) * mm});
            skArc(sketch, "E38.0.292", {"start": v(-36.5, 9.79) * mm, "mid": v(-36.82, 9.84) * mm, "end": v(-37.13, 9.83) * mm});
            skArc(sketch, "E38.0.293", {"start": v(-37.13, 9.83) * mm, "mid": v(-38.67, 9.48) * mm, "end": v(-40.13, 8.88) * mm});
            skArc(sketch, "E38.0.294", {"start": v(-40.13, 8.88) * mm, "mid": v(-40.3, 8.75) * mm, "end": v(-40.39, 8.56) * mm});
            skLineSegment(sketch, "E38.0.295", {"start": v(-40.39, 8.56) * mm, "end": v(-40.52, 8.06) * mm});
            skLineSegment(sketch, "E38.0.296", {"start": v(-40.52, 8.06) * mm, "end": v(-40.6, 7.55) * mm});
            skArc(sketch, "E38.0.297", {"start": v(-40.6, 7.55) * mm, "mid": v(-40.57, 7.34) * mm, "end": v(-40.47, 7.15) * mm});
            skArc(sketch, "E38.0.298", {"start": v(-40.47, 7.15) * mm, "mid": v(-39.36, 6.04) * mm, "end": v(-38.07, 5.13) * mm});
            skArc(sketch, "E38.0.299", {"start": v(-38.07, 5.13) * mm, "mid": v(-37.78, 5) * mm, "end": v(-37.47, 4.92) * mm});
            skLineSegment(sketch, "E38.0.300", {"start": v(-37.47, 4.92) * mm, "end": v(-36.17, 4.75) * mm});
            skArc(sketch, "E38.0.301", {"start": v(-36.17, 4.75) * mm, "mid": v(-35.14, 4.17) * mm, "end": v(-34.8, 3.04) * mm});
            skArc(sketch, "E38.0.302", {"start": v(-34.8, 3.04) * mm, "mid": v(-34.85, 2.28) * mm, "end": v(-34.9, 1.53) * mm});
            skArc(sketch, "E38.0.303", {"start": v(-34.9, 1.53) * mm, "mid": v(-35.38, 0.45) * mm, "end": v(-36.48, 0) * mm});
            skLineSegment(sketch, "E38.0.304", {"start": v(-36.48, 0) * mm, "end": v(-37.8, 0) * mm});
            skArc(sketch, "E38.0.305", {"start": v(-37.8, 0) * mm, "mid": v(-38.1, -0.02) * mm, "end": v(-38.41, -0.12) * mm});
            skArc(sketch, "E38.0.306", {"start": v(-38.41, -0.12) * mm, "mid": v(-39.8, -0.85) * mm, "end": v(-41.06, -1.8) * mm});
            skArc(sketch, "E38.0.307", {"start": v(-41.06, -1.8) * mm, "mid": v(-41.18, -1.98) * mm, "end": v(-41.23, -2.18) * mm});
            skLineSegment(sketch, "E38.0.308", {"start": v(-41.23, -2.18) * mm, "end": v(-41.23, -2.7) * mm});
            skLineSegment(sketch, "E38.0.309", {"start": v(-41.23, -2.7) * mm, "end": v(-41.16, -3.22) * mm});
            skArc(sketch, "E38.0.310", {"start": v(-41.16, -3.22) * mm, "mid": v(-41.1, -3.41) * mm, "end": v(-40.95, -3.57) * mm});
            skArc(sketch, "E38.0.311", {"start": v(-40.95, -3.57) * mm, "mid": v(-39.58, -4.35) * mm, "end": v(-38.1, -4.9) * mm});
            skSolve(sketch);
        }
        {
            var Q0;
            Q0=makeQuery(id+"F0.imprint","IMPRINT",FACE,{"disambiguationData":[TD([[makeQuery(id+"F0.imprint","IMPRINT",EDGE,{"derivedFrom":sQuery(id+"F0.wireOp",EDGE,"E0")}),1.0]])]});
            var Q1;
            Q1=makeQuery(id+"F2.imprint","IMPRINT",FACE,{"disambiguationData":[TD([[makeQuery(id+"F2.imprint","IMPRINT",EDGE,{"derivedFrom":sQuery(id+"F2.wireOp",EDGE,"E38.0.0")}),1.0]])]});
            var Q2;
            Q2=sQuery(id+"F2.wireOp",VERTEX,"E38.0.214.start");
            var Q3;
            Q3=sQuery(id+"F0.wireOp",VERTEX,"E3.start");
            loft(context, id + "F3", {"sheetProfilesArray" : [{ "sheetProfileEntities" : qUnion([Q0]) }, { "sheetProfileEntities" : qUnion([Q1]) }], "matchConnections" : true, "connections" : [{ "connectionEntities" : qUnion([Q2, Q3]), "connectionEdgeQueries" : qUnion([]), "connectionEdgeParameters" : [] }]});
        }
        {
            var Q0;
            Q0=makeQuery(id+"F3.opLoft","CAP_FACE",FACE,{"disambiguationData":[OSD([makeQuery(id+"F2.imprint","IMPRINT",FACE,{"disambiguationData":[TD([[makeQuery(id+"F2.imprint","IMPRINT",EDGE,{"derivedFrom":sQuery(id+"F2.wireOp",EDGE,"E38.0.0")}),1.0]])]})])],"isStart":true});
            var sketch = newSketch(context, id + "F4", { "sketchPlane" : qUnion([Q0])});
            skPoint(sketch, "E39", {"position": v(0, 0) * mm});
            skSolve(sketch);
        }
        {
            var Q0;
            Q0=sQuery(id+"F4.wireOp",VERTEX,"E39");
            var Q1;
            Q1=makeQuery(id+"F3.opLoft","SWEPT_BODY",BODY,{"disambiguationData":[OSD([makeQuery(id+"F0.imprint","IMPRINT",FACE,{"disambiguationData":[TD([[makeQuery(id+"F0.imprint","IMPRINT",EDGE,{"derivedFrom":sQuery(id+"F0.wireOp",EDGE,"E0")}),1.0]])]}),makeQuery(id+"F2.imprint","IMPRINT",FACE,{"disambiguationData":[TD([[makeQuery(id+"F2.imprint","IMPRINT",EDGE,{"derivedFrom":sQuery(id+"F2.wireOp",EDGE,"E38.0.0")}),1.0]])]})])]});
            hole(context, id + "F5", {"style" : HoleStyle.SIMPLE, "endStyle" : HoleEndStyle.THROUGH, "holeDiameter" : 12.7 * mm, "tappedDepth" : 12.7 * mm, "tapClearance" : 3, "locations" : qUnion([Q0]), "scope" : qUnion([Q1])});
        }
    });
